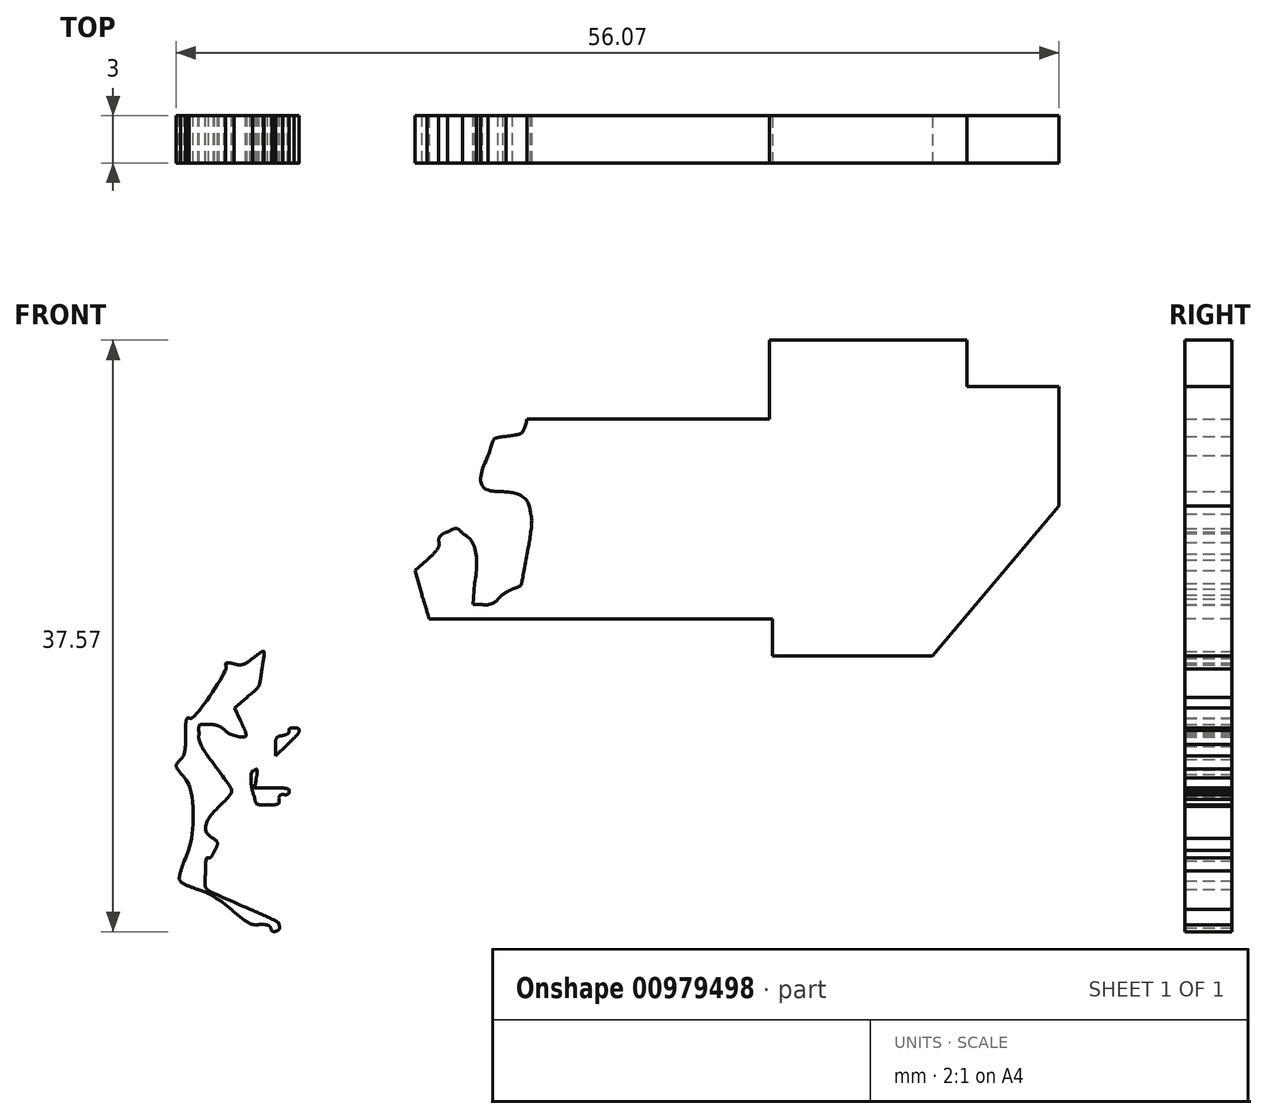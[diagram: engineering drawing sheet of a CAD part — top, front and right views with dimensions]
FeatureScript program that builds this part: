
annotation { "Feature Type Name" : "Feature", "Feature Type Description" : "" }
export const myFeature = defineFeature(function(context is Context, id is Id, definition is map)
    precondition{}
    {
        {
            var Q0;
            Q0=qCreatedBy(makeId("Front.planeOp"),FACE);
            var sketch = newSketch(context, id + "F0", { "sketchPlane" : qUnion([Q0])});
            skLineSegment(sketch, "E0", {"start": v(-32.88, 19.2) * mm, "end": v(-32.1, 20.83) * mm});
            skLineSegment(sketch, "E1", {"start": v(-32.1, 20.83) * mm, "end": v(-32.57, 22.16) * mm});
            skLineSegment(sketch, "E2", {"start": v(-27.5, 16.63) * mm, "end": v(-26.83, 16.28) * mm});
            skLineSegment(sketch, "E3", {"start": v(-26.83, 16.28) * mm, "end": v(-26.97, 16.83) * mm});
            skLineSegment(sketch, "E4", {"start": v(-24.85, 15.67) * mm, "end": v(-25.4, 15.88) * mm});
            skLineSegment(sketch, "E5", {"start": v(-25.4, 15.88) * mm, "end": v(-25.34, 18.4) * mm});
            skLineSegment(sketch, "E6", {"start": v(-1.75, 78.04) * mm, "end": v(-0.2, 79.6) * mm});
            skLineSegment(sketch, "E7", {"start": v(-0.2, 79.6) * mm, "end": v(1.27, 79.6) * mm});
            skLineSegment(sketch, "E8", {"start": v(38.3, 44.26) * mm, "end": v(38.3, 43.17) * mm});
            skLineSegment(sketch, "E9", {"start": v(38.3, 43.17) * mm, "end": v(37.62, 43.24) * mm});
            skLineSegment(sketch, "E10", {"start": v(39.65, -31.25) * mm, "end": v(39.52, -33.83) * mm});
            skLineSegment(sketch, "E11", {"start": v(39.52, -33.83) * mm, "end": v(40.18, -34.42) * mm});
            skLineSegment(sketch, "E12", {"start": v(1.4, 79.08) * mm, "end": v(0.3, 79.22) * mm});
            skLineSegment(sketch, "E13", {"start": v(0.3, 79.22) * mm, "end": v(-1.23, 77.67) * mm});
            skLineSegment(sketch, "E14", {"start": v(-12.51, 69.45) * mm, "end": v(-13.4, 69.45) * mm});
            skLineSegment(sketch, "E15", {"start": v(-13.4, 69.45) * mm, "end": v(-13.27, 67.07) * mm});
            skLineSegment(sketch, "E16", {"start": v(-18.31, 54.9) * mm, "end": v(-18.88, 53.48) * mm});
            skLineSegment(sketch, "E17", {"start": v(-18.88, 53.48) * mm, "end": v(-18.43, 53.1) * mm});
            skLineSegment(sketch, "E18", {"start": v(-20.94, 40.45) * mm, "end": v(-21.55, 40.45) * mm});
            skLineSegment(sketch, "E19", {"start": v(-21.55, 40.45) * mm, "end": v(-21.44, 41.8) * mm});
            skLineSegment(sketch, "E20", {"start": v(-24.47, 43.3) * mm, "end": v(-25.23, 42.61) * mm});
            skLineSegment(sketch, "E21", {"start": v(-25.23, 42.61) * mm, "end": v(-24.8, 41.05) * mm});
            skLineSegment(sketch, "E22", {"start": v(-37.96, -16.18) * mm, "end": v(-37.29, -17.23) * mm});
            skLineSegment(sketch, "E23", {"start": v(-37.29, -17.23) * mm, "end": v(-37.41, -20.41) * mm});
            skLineSegment(sketch, "E24", {"start": v(-30.4, -60.92) * mm, "end": v(-31.42, -62.04) * mm});
            skLineSegment(sketch, "E25", {"start": v(-31.42, -62.04) * mm, "end": v(-30.9, -63.02) * mm});
            skLineSegment(sketch, "E26", {"start": v(-36.35, 33.14) * mm, "end": v(-36.7, 33.88) * mm});
            skLineSegment(sketch, "E27", {"start": v(-36.7, 33.88) * mm, "end": v(-35.92, 34.57) * mm});
            skLineSegment(sketch, "E28", {"start": v(-34.09, 31.43) * mm, "end": v(-34.09, 30.84) * mm});
            skLineSegment(sketch, "E29", {"start": v(-34.09, 30.84) * mm, "end": v(-33.35, 31.56) * mm});
            skFitSpline(sketch, "E30", {"points": [v(-13.45, -80.7) * mm, v(-14.26, -80.4) * mm, v(-15.79, -79.86) * mm, v(-16.84, -79.51) * mm]});
            skFitSpline(sketch, "E31", {"points": [v(-16.84, -79.51) * mm, v(-20.43, -78.33) * mm, v(-20.6, -78.25) * mm, v(-21.55, -77.26) * mm]});
            skFitSpline(sketch, "E32", {"points": [v(-21.55, -77.26) * mm, v(-22.07, -76.72) * mm, v(-23.66, -74.52) * mm, v(-25.09, -72.37) * mm]});
            skFitSpline(sketch, "E33", {"points": [v(-25.09, -72.37) * mm, v(-26.52, -70.21) * mm, v(-28.36, -67.6) * mm, v(-29.19, -66.55) * mm]});
            skFitSpline(sketch, "E34", {"points": [v(-29.19, -66.55) * mm, v(-30.6, -64.76) * mm, v(-31.97, -62.53) * mm, v(-31.97, -62.03) * mm]});
            skFitSpline(sketch, "E35", {"points": [v(-31.97, -62.03) * mm, v(-31.97, -61.91) * mm, v(-31.5, -61.27) * mm, v(-30.92, -60.6) * mm]});
            skFitSpline(sketch, "E36", {"points": [v(-30.92, -60.6) * mm, v(-29.85, -59.39) * mm, v(-29, -57.92) * mm, v(-29, -57.28) * mm]});
            skFitSpline(sketch, "E37", {"points": [v(-29, -57.28) * mm, v(-29, -57.08) * mm, v(-29.34, -56.3) * mm, v(-29.75, -55.53) * mm]});
            skFitSpline(sketch, "E38", {"points": [v(-29.75, -55.53) * mm, v(-30.57, -53.98) * mm, v(-30.63, -53.57) * mm, v(-30.2, -52.72) * mm]});
            skFitSpline(sketch, "E39", {"points": [v(-30.2, -52.72) * mm, v(-29.95, -52.26) * mm, v(-29.92, -51.55) * mm, v(-30.04, -49.29) * mm]});
            skFitSpline(sketch, "E40", {"points": [v(-30.04, -49.29) * mm, v(-30.2, -46.13) * mm, v(-30.12, -46.32) * mm, v(-32.34, -43.6) * mm]});
            skFitSpline(sketch, "E41", {"points": [v(-32.34, -43.6) * mm, v(-32.83, -43) * mm, v(-33.38, -42.01) * mm, v(-33.55, -41.42) * mm]});
            skFitSpline(sketch, "E42", {"points": [v(-33.55, -41.42) * mm, v(-33.73, -40.84) * mm, v(-34.2, -39.94) * mm, v(-34.62, -39.44) * mm]});
            skFitSpline(sketch, "E43", {"points": [v(-34.62, -39.44) * mm, v(-36.03, -37.71) * mm, v(-36.52, -35.97) * mm, v(-35.98, -34.56) * mm]});
            skFitSpline(sketch, "E44", {"points": [v(-35.98, -34.56) * mm, v(-35.86, -34.24) * mm, v(-35.38, -33.57) * mm, v(-34.92, -33.07) * mm]});
            skFitSpline(sketch, "E45", {"points": [v(-34.92, -33.07) * mm, v(-33.97, -32.03) * mm, v(-34, -32.17) * mm, v(-34.37, -30.78) * mm]});
            skFitSpline(sketch, "E46", {"points": [v(-34.37, -30.78) * mm, v(-34.75, -29.38) * mm, v(-35.2, -28.53) * mm, v(-36.46, -26.88) * mm]});
            skFitSpline(sketch, "E47", {"points": [v(-36.46, -26.88) * mm, v(-37.04, -26.13) * mm, v(-37.61, -25.27) * mm, v(-37.73, -24.97) * mm]});
            skFitSpline(sketch, "E48", {"points": [v(-37.73, -24.97) * mm, v(-37.97, -24.39) * mm, v(-38.06, -21.07) * mm, v(-37.9, -18.8) * mm]});
            skFitSpline(sketch, "E49", {"points": [v(-37.9, -18.8) * mm, v(-37.82, -17.55) * mm, v(-37.87, -17.35) * mm, v(-38.39, -16.67) * mm]});
            skFitSpline(sketch, "E50", {"points": [v(-38.39, -16.67) * mm, v(-39.51, -15.19) * mm, v(-39.6, -12.77) * mm, v(-38.72, -7.81) * mm]});
            skFitSpline(sketch, "E51", {"points": [v(-38.72, -7.81) * mm, v(-38.24, -5.14) * mm, v(-38.31, -2.1) * mm, v(-38.87, -1) * mm]});
            skFitSpline(sketch, "E52", {"points": [v(-38.87, -1) * mm, v(-39.1, -0.56) * mm, v(-39.11, -0.29) * mm, v(-38.94, 0.17) * mm]});
            skFitSpline(sketch, "E53", {"points": [v(-38.94, 0.17) * mm, v(-38.62, 1) * mm, v(-38.87, 3.38) * mm, v(-39.5, 5.38) * mm]});
            skFitSpline(sketch, "E54", {"points": [v(-39.5, 5.38) * mm, v(-39.78, 6.29) * mm, v(-40.01, 7.26) * mm, v(-40.01, 7.54) * mm]});
            skFitSpline(sketch, "E55", {"points": [v(-40.01, 7.54) * mm, v(-40.01, 7.83) * mm, v(-39.68, 9.05) * mm, v(-39.27, 10.27) * mm]});
            skFitSpline(sketch, "E56", {"points": [v(-39.27, 10.27) * mm, v(-38.41, 12.85) * mm, v(-38.39, 13.06) * mm, v(-38.96, 13.2) * mm]});
            skFitSpline(sketch, "E57", {"points": [v(-38.96, 13.2) * mm, v(-39.71, 13.4) * mm, v(-39.48, 14.32) * mm, v(-38.38, 15.5) * mm]});
            skFitSpline(sketch, "E58", {"points": [v(-38.38, 15.5) * mm, v(-36.83, 17.16) * mm, v(-35.68, 17.57) * mm, v(-34.74, 16.8) * mm]});
            skFitSpline(sketch, "E59", {"points": [v(-34.74, 16.8) * mm, v(-34.08, 16.26) * mm, v(-32.77, 13.22) * mm, v(-32.66, 11.98) * mm]});
            skFitSpline(sketch, "E60", {"points": [v(-32.66, 11.98) * mm, v(-32.55, 10.86) * mm, v(-32.37, 10.61) * mm, v(-31.6, 10.6) * mm]});
            skFitSpline(sketch, "E61", {"points": [v(-31.6, 10.6) * mm, v(-31, 10.6) * mm, v(-30.96, 11.24) * mm, v(-31.55, 11.77) * mm]});
            skFitSpline(sketch, "E62", {"points": [v(-31.55, 11.77) * mm, v(-31.84, 12.03) * mm, v(-31.97, 12.42) * mm, v(-31.97, 13) * mm]});
            skFitSpline(sketch, "E63", {"points": [v(-31.97, 13) * mm, v(-31.97, 14.32) * mm, v(-32.62, 16.12) * mm, v(-33.18, 16.38) * mm]});
            skFitSpline(sketch, "E64", {"points": [v(-33.18, 16.38) * mm, v(-33.86, 16.69) * mm, v(-33.8, 17.27) * mm, v(-32.88, 19.2) * mm]});
            skFitSpline(sketch, "E65", {"points": [v(-32.57, 22.16) * mm, v(-32.82, 22.9) * mm, v(-33.03, 23.65) * mm, v(-33.03, 23.83) * mm]});
            skFitSpline(sketch, "E66", {"points": [v(-33.03, 23.83) * mm, v(-33.03, 24.1) * mm, v(-33.14, 24.14) * mm, v(-33.5, 24.01) * mm]});
            skFitSpline(sketch, "E67", {"points": [v(-33.5, 24.01) * mm, v(-33.77, 23.92) * mm, v(-34.4, 23.84) * mm, v(-34.93, 23.84) * mm]});
            skFitSpline(sketch, "E68", {"points": [v(-34.93, 23.84) * mm, v(-35.84, 23.83) * mm, v(-35.89, 23.86) * mm, v(-35.95, 24.48) * mm]});
            skFitSpline(sketch, "E69", {"points": [v(-35.95, 24.48) * mm, v(-36.05, 25.55) * mm, v(-34.78, 26.27) * mm, v(-32.78, 26.27) * mm]});
            skFitSpline(sketch, "E70", {"points": [v(-32.78, 26.27) * mm, v(-31.93, 26.27) * mm, v(-31.64, 26.16) * mm, v(-31.1, 25.65) * mm]});
            skFitSpline(sketch, "E71", {"points": [v(-31.1, 25.65) * mm, v(-30.75, 25.3) * mm, v(-30.32, 25.08) * mm, v(-30.15, 25.14) * mm]});
            skFitSpline(sketch, "E72", {"points": [v(-30.15, 25.14) * mm, v(-29.7, 25.31) * mm, v(-29.77, 25.47) * mm, v(-30.7, 26.37) * mm]});
            skFitSpline(sketch, "E73", {"points": [v(-30.7, 26.37) * mm, v(-31.5, 27.15) * mm, v(-31.55, 27.27) * mm, v(-31.55, 28.43) * mm]});
            skFitSpline(sketch, "E74", {"points": [v(-31.55, 28.43) * mm, v(-31.55, 29.6) * mm, v(-31.52, 29.65) * mm, v(-31.02, 29.65) * mm]});
            skFitSpline(sketch, "E75", {"points": [v(-31.02, 29.65) * mm, v(-30.7, 29.65) * mm, v(-30.49, 29.53) * mm, v(-30.49, 29.36) * mm]});
            skFitSpline(sketch, "E76", {"points": [v(-30.49, 29.36) * mm, v(-30.49, 28.94) * mm, v(-28.82, 27.75) * mm, v(-28.24, 27.75) * mm]});
            skFitSpline(sketch, "E77", {"points": [v(-28.24, 27.75) * mm, v(-27.83, 27.75) * mm, v(-27.75, 27.6) * mm, v(-27.62, 26.6) * mm]});
            skFitSpline(sketch, "E78", {"points": [v(-27.62, 26.6) * mm, v(-27.46, 25.26) * mm, v(-27.66, 24.55) * mm, v(-28.57, 23.22) * mm]});
            skFitSpline(sketch, "E79", {"points": [v(-28.57, 23.22) * mm, v(-29.21, 22.29) * mm, v(-29.4, 21.61) * mm, v(-29.02, 21.61) * mm]});
            skFitSpline(sketch, "E80", {"points": [v(-29.02, 21.61) * mm, v(-28.66, 21.61) * mm, v(-28.35, 20.18) * mm, v(-28.49, 19.14) * mm]});
            skFitSpline(sketch, "E81", {"points": [v(-28.49, 19.14) * mm, v(-28.66, 17.84) * mm, v(-28.36, 17.07) * mm, v(-27.5, 16.63) * mm]});
            skFitSpline(sketch, "E82", {"points": [v(-26.97, 16.83) * mm, v(-27.1, 17.33) * mm, v(-27.05, 17.38) * mm, v(-26.5, 17.38) * mm]});
            skFitSpline(sketch, "E83", {"points": [v(-26.5, 17.38) * mm, v(-25.81, 17.38) * mm, v(-25.62, 17.08) * mm, v(-25.62, 16.04) * mm]});
            skFitSpline(sketch, "E84", {"points": [v(-25.62, 16.04) * mm, v(-25.62, 15.5) * mm, v(-25.82, 15.19) * mm, v(-26.56, 14.52) * mm]});
            skFitSpline(sketch, "E85", {"points": [v(-26.56, 14.52) * mm, v(-27.09, 14.05) * mm, v(-27.58, 13.4) * mm, v(-27.66, 13.06) * mm]});
            skFitSpline(sketch, "E86", {"points": [v(-27.66, 13.06) * mm, v(-27.79, 12.49) * mm, v(-27.76, 12.45) * mm, v(-27.3, 12.58) * mm]});
            skFitSpline(sketch, "E87", {"points": [v(-27.3, 12.58) * mm, v(-27.01, 12.65) * mm, v(-26.47, 12.72) * mm, v(-26.09, 12.72) * mm]});
            skFitSpline(sketch, "E88", {"points": [v(-26.09, 12.72) * mm, v(-25.47, 12.72) * mm, v(-25.42, 12.76) * mm, v(-25.61, 13.13) * mm]});
            skFitSpline(sketch, "E89", {"points": [v(-25.61, 13.13) * mm, v(-26.02, 13.88) * mm, v(-25.88, 14.6) * mm, v(-25.31, 14.75) * mm]});
            skFitSpline(sketch, "E90", {"points": [v(-25.31, 14.75) * mm, v(-25.03, 14.82) * mm, v(-24.68, 15.01) * mm, v(-24.55, 15.17) * mm]});
            skFitSpline(sketch, "E91", {"points": [v(-24.55, 15.17) * mm, v(-24.35, 15.4) * mm, v(-24.42, 15.5) * mm, v(-24.85, 15.67) * mm]});
            skFitSpline(sketch, "E92", {"points": [v(-25.34, 18.4) * mm, v(-25.28, 20.49) * mm, v(-25.2, 21.05) * mm, v(-24.84, 21.66) * mm]});
            skFitSpline(sketch, "E93", {"points": [v(-24.84, 21.66) * mm, v(-24.6, 22.07) * mm, v(-24.33, 22.91) * mm, v(-24.25, 23.54) * mm]});
            skFitSpline(sketch, "E94", {"points": [v(-24.25, 23.54) * mm, v(-24.05, 24.98) * mm, v(-23.67, 25.42) * mm, v(-22.64, 25.42) * mm]});
            skFitSpline(sketch, "E95", {"points": [v(-22.64, 25.42) * mm, v(-21.97, 25.42) * mm, v(-21.73, 25.28) * mm, v(-21.09, 24.54) * mm]});
            skFitSpline(sketch, "E96", {"points": [v(-21.09, 24.54) * mm, v(-20.67, 24.05) * mm, v(-20.32, 23.55) * mm, v(-20.32, 23.43) * mm]});
            skFitSpline(sketch, "E97", {"points": [v(-20.32, 23.43) * mm, v(-20.3, 22.93) * mm, v(-19.5, 25.15) * mm, v(-19.5, 25.74) * mm]});
            skFitSpline(sketch, "E98", {"points": [v(-19.5, 25.74) * mm, v(-19.48, 26.68) * mm, v(-19.75, 27) * mm, v(-20.27, 26.68) * mm]});
            skFitSpline(sketch, "E99", {"points": [v(-20.27, 26.68) * mm, v(-20.84, 26.32) * mm, v(-23.7, 26.75) * mm, v(-24.99, 27.38) * mm]});
            skFitSpline(sketch, "E100", {"points": [v(-24.99, 27.38) * mm, v(-26.7, 28.23) * mm, v(-27.27, 29.95) * mm, v(-26.55, 32.07) * mm]});
            skFitSpline(sketch, "E101", {"points": [v(-26.55, 32.07) * mm, v(-26.23, 33) * mm, v(-26.23, 33.13) * mm, v(-26.58, 33.9) * mm]});
            skFitSpline(sketch, "E102", {"points": [v(-26.58, 33.9) * mm, v(-27.04, 34.91) * mm, v(-26.9, 36) * mm, v(-26.2, 36.92) * mm]});
            skFitSpline(sketch, "E103", {"points": [v(-26.2, 36.92) * mm, v(-24.96, 38.54) * mm, v(-24.76, 39.42) * mm, v(-25.3, 40.73) * mm]});
            skFitSpline(sketch, "E104", {"points": [v(-25.3, 40.73) * mm, v(-25.48, 41.15) * mm, v(-25.62, 41.87) * mm, v(-25.62, 42.33) * mm]});
            skFitSpline(sketch, "E105", {"points": [v(-25.62, 42.33) * mm, v(-25.62, 43.02) * mm, v(-25.5, 43.25) * mm, v(-24.99, 43.62) * mm]});
            skFitSpline(sketch, "E106", {"points": [v(-24.99, 43.62) * mm, v(-24.64, 43.87) * mm, v(-24.35, 44.26) * mm, v(-24.35, 44.48) * mm]});
            skFitSpline(sketch, "E107", {"points": [v(-24.35, 44.48) * mm, v(-24.35, 45.6) * mm, v(-22.43, 46.16) * mm, v(-21.62, 45.29) * mm]});
            skFitSpline(sketch, "E108", {"points": [v(-21.62, 45.29) * mm, v(-21.1, 44.74) * mm, v(-20.66, 42.78) * mm, v(-20.82, 41.8) * mm]});
            skFitSpline(sketch, "E109", {"points": [v(-20.82, 41.8) * mm, v(-20.95, 40.98) * mm, v(-20.5, 40.8) * mm, v(-20.12, 41.5) * mm]});
            skFitSpline(sketch, "E110", {"points": [v(-20.12, 41.5) * mm, v(-20, 41.74) * mm, v(-19.7, 41.93) * mm, v(-19.48, 41.93) * mm]});
            skFitSpline(sketch, "E111", {"points": [v(-19.48, 41.93) * mm, v(-19.2, 41.93) * mm, v(-19.03, 42.12) * mm, v(-18.95, 42.51) * mm]});
            skFitSpline(sketch, "E112", {"points": [v(-18.95, 42.51) * mm, v(-18.9, 42.83) * mm, v(-18.75, 43.5) * mm, v(-18.63, 44) * mm]});
            skFitSpline(sketch, "E113", {"points": [v(-18.63, 44) * mm, v(-18.15, 46.1) * mm, v(-18.46, 46.83) * mm, v(-19.95, 47.1) * mm]});
            skFitSpline(sketch, "E114", {"points": [v(-19.95, 47.1) * mm, v(-21.37, 47.35) * mm, v(-21.68, 48.31) * mm, v(-21.02, 50.45) * mm]});
            skFitSpline(sketch, "E115", {"points": [v(-21.02, 50.45) * mm, v(-20.67, 51.58) * mm, v(-20.6, 51.66) * mm, v(-20, 51.67) * mm]});
            skFitSpline(sketch, "E116", {"points": [v(-20, 51.67) * mm, v(-19.64, 51.67) * mm, v(-19.17, 51.8) * mm, v(-18.94, 51.97) * mm]});
            skFitSpline(sketch, "E117", {"points": [v(-18.94, 51.97) * mm, v(-18.56, 52.25) * mm, v(-18.55, 52.28) * mm, v(-18.9, 52.67) * mm]});
            skFitSpline(sketch, "E118", {"points": [v(-18.9, 52.67) * mm, v(-19.36, 53.18) * mm, v(-19.37, 53.99) * mm, v(-18.93, 55) * mm]});
            skFitSpline(sketch, "E119", {"points": [v(-18.93, 55) * mm, v(-18.26, 56.57) * mm, v(-18.22, 56.96) * mm, v(-18.55, 58.71) * mm]});
            skFitSpline(sketch, "E120", {"points": [v(-18.55, 58.71) * mm, v(-19.05, 61.35) * mm, v(-18.66, 63.1) * mm, v(-17.57, 63.1) * mm]});
            skFitSpline(sketch, "E121", {"points": [v(-17.57, 63.1) * mm, v(-17.13, 63.1) * mm, v(-16.93, 62.86) * mm, v(-16.62, 61.94) * mm]});
            skFitSpline(sketch, "E122", {"points": [v(-16.62, 61.94) * mm, v(-16.19, 60.62) * mm, v(-15.25, 61.36) * mm, v(-15.25, 63.03) * mm]});
            skFitSpline(sketch, "E123", {"points": [v(-15.25, 63.03) * mm, v(-15.25, 63.72) * mm, v(-15.21, 63.77) * mm, v(-14.72, 63.65) * mm]});
            skFitSpline(sketch, "E124", {"points": [v(-14.72, 63.65) * mm, v(-13.88, 63.44) * mm, v(-13.7, 64.21) * mm, v(-13.86, 67.25) * mm]});
            skFitSpline(sketch, "E125", {"points": [v(-13.86, 67.25) * mm, v(-14.01, 70.15) * mm, v(-14.06, 70.07) * mm, v(-12.21, 70.08) * mm]});
            skFitSpline(sketch, "E126", {"points": [v(-12.21, 70.08) * mm, v(-11.52, 70.08) * mm, v(-11.25, 70.23) * mm, v(-10.4, 71.12) * mm]});
            skFitSpline(sketch, "E127", {"points": [v(-10.4, 71.12) * mm, v(-9.38, 72.18) * mm, v(-9.03, 72.34) * mm, v(-6.52, 72.84) * mm]});
            skFitSpline(sketch, "E128", {"points": [v(-6.52, 72.84) * mm, v(-4.93, 73.15) * mm, v(-4.21, 73.78) * mm, v(-3.7, 75.27) * mm]});
            skFitSpline(sketch, "E129", {"points": [v(-3.7, 75.27) * mm, v(-3.38, 76.2) * mm, v(-2.96, 76.8) * mm, v(-1.75, 78.04) * mm]});
            skFitSpline(sketch, "E130", {"points": [v(1.27, 79.6) * mm, v(2.66, 79.6) * mm, v(2.79, 79.65) * mm, v(3.57, 80.36) * mm]});
            skFitSpline(sketch, "E131", {"points": [v(3.57, 80.36) * mm, v(4.72, 81.4) * mm, v(5.62, 81.51) * mm, v(6.84, 80.8) * mm]});
            skFitSpline(sketch, "E132", {"points": [v(6.84, 80.8) * mm, v(7.4, 80.48) * mm, v(8.11, 80.24) * mm, v(8.56, 80.24) * mm]});
            skFitSpline(sketch, "E133", {"points": [v(8.56, 80.24) * mm, v(9.65, 80.24) * mm, v(10.66, 79.76) * mm, v(12.03, 78.58) * mm]});
            skFitSpline(sketch, "E134", {"points": [v(12.03, 78.58) * mm, v(12.68, 78.02) * mm, v(13.76, 77.21) * mm, v(14.43, 76.8) * mm]});
            skFitSpline(sketch, "E135", {"points": [v(14.43, 76.8) * mm, v(16.07, 75.75) * mm, v(16.3, 75.23) * mm, v(16.26, 72.68) * mm]});
            skFitSpline(sketch, "E136", {"points": [v(16.26, 72.68) * mm, v(16.21, 70.3) * mm, v(16.3, 70.06) * mm, v(17.99, 67.97) * mm]});
            skFitSpline(sketch, "E137", {"points": [v(17.99, 67.97) * mm, v(19.34, 66.28) * mm, v(19.58, 65.73) * mm, v(19.78, 63.84) * mm]});
            skFitSpline(sketch, "E138", {"points": [v(19.78, 63.84) * mm, v(19.97, 61.97) * mm, v(20.1, 61.75) * mm, v(21.2, 61.28) * mm]});
            skFitSpline(sketch, "E139", {"points": [v(21.2, 61.28) * mm, v(21.95, 60.97) * mm, v(22.77, 60.9) * mm, v(25.95, 60.87) * mm]});
            skFitSpline(sketch, "E140", {"points": [v(25.95, 60.87) * mm, v(29.47, 60.83) * mm, v(29.87, 60.8) * mm, v(30.78, 60.35) * mm]});
            skFitSpline(sketch, "E141", {"points": [v(30.78, 60.35) * mm, v(31.33, 60.09) * mm, v(31.82, 59.71) * mm, v(31.88, 59.53) * mm]});
            skFitSpline(sketch, "E142", {"points": [v(31.88, 59.53) * mm, v(32.1, 58.78) * mm, v(32.32, 58.58) * mm, v(33.34, 58.19) * mm]});
            skFitSpline(sketch, "E143", {"points": [v(33.34, 58.19) * mm, v(35, 57.54) * mm, v(35.47, 56.96) * mm, v(35.61, 55.41) * mm]});
            skFitSpline(sketch, "E144", {"points": [v(35.61, 55.41) * mm, v(35.68, 54.7) * mm, v(35.93, 53.67) * mm, v(36.17, 53.15) * mm]});
            skFitSpline(sketch, "E145", {"points": [v(36.17, 53.15) * mm, v(36.4, 52.63) * mm, v(36.6, 51.94) * mm, v(36.6, 51.62) * mm]});
            skFitSpline(sketch, "E146", {"points": [v(36.6, 51.62) * mm, v(36.6, 51.3) * mm, v(36.8, 50.55) * mm, v(37.02, 49.93) * mm]});
            skFitSpline(sketch, "E147", {"points": [v(37.02, 49.93) * mm, v(37.7, 48.08) * mm, v(38.3, 45.42) * mm, v(38.3, 44.26) * mm]});
            skFitSpline(sketch, "E148", {"points": [v(37.62, 43.24) * mm, v(36.87, 43.31) * mm, v(36.86, 43.33) * mm, v(36.05, 46.9) * mm]});
            skFitSpline(sketch, "E149", {"points": [v(36.05, 46.9) * mm, v(35.75, 48.23) * mm, v(35.65, 48.45) * mm, v(35.6, 47.92) * mm]});
            skFitSpline(sketch, "E150", {"points": [v(35.6, 47.92) * mm, v(35.56, 47.55) * mm, v(35.72, 46.61) * mm, v(35.96, 45.84) * mm]});
            skFitSpline(sketch, "E151", {"points": [v(35.96, 45.84) * mm, v(36.2, 45.06) * mm, v(36.4, 44.16) * mm, v(36.4, 43.83) * mm]});
            skFitSpline(sketch, "E152", {"points": [v(36.4, 43.83) * mm, v(36.4, 42.72) * mm, v(36.23, 42.57) * mm, v(35.04, 42.57) * mm]});
            skFitSpline(sketch, "E153", {"points": [v(35.04, 42.57) * mm, v(34.35, 42.57) * mm, v(33.78, 42.44) * mm, v(33.53, 42.23) * mm]});
            skFitSpline(sketch, "E154", {"points": [v(33.53, 42.23) * mm, v(33.14, 41.92) * mm, v(33.15, 41.9) * mm, v(33.78, 42.01) * mm]});
            skFitSpline(sketch, "E155", {"points": [v(33.78, 42.01) * mm, v(34.37, 42.1) * mm, v(34.48, 42.05) * mm, v(34.7, 41.5) * mm]});
            skFitSpline(sketch, "E156", {"points": [v(34.7, 41.5) * mm, v(35.23, 40.23) * mm, v(34.46, 39.89) * mm, v(32.77, 40.66) * mm]});
            skFitSpline(sketch, "E157", {"points": [v(32.77, 40.66) * mm, v(30, 41.91) * mm, v(30.46, 40.26) * mm, v(33.3, 38.77) * mm]});
            skFitSpline(sketch, "E158", {"points": [v(33.3, 38.77) * mm, v(34.7, 38.04) * mm, v(35.03, 37.98) * mm, v(35.2, 38.44) * mm]});
            skFitSpline(sketch, "E159", {"points": [v(35.2, 38.44) * mm, v(35.4, 38.97) * mm, v(36.94, 38.86) * mm, v(37.34, 38.29) * mm]});
            skFitSpline(sketch, "E160", {"points": [v(37.34, 38.29) * mm, v(37.8, 37.64) * mm, v(37.75, 36.5) * mm, v(37.25, 35.69) * mm]});
            skFitSpline(sketch, "E161", {"points": [v(37.25, 35.69) * mm, v(37.01, 35.31) * mm, v(36.68, 34.6) * mm, v(36.5, 34.09) * mm]});
            skFitSpline(sketch, "E162", {"points": [v(36.5, 34.09) * mm, v(36.07, 32.87) * mm, v(35.62, 32.4) * mm, v(34.86, 32.4) * mm]});
            skFitSpline(sketch, "E163", {"points": [v(34.86, 32.4) * mm, v(34.06, 32.4) * mm, v(32.85, 32.98) * mm, v(32.57, 33.5) * mm]});
            skFitSpline(sketch, "E164", {"points": [v(32.57, 33.5) * mm, v(32.35, 33.9) * mm, v(32.37, 33.91) * mm, v(33.4, 34.23) * mm]});
            skFitSpline(sketch, "E165", {"points": [v(33.4, 34.23) * mm, v(33.55, 34.27) * mm, v(33.64, 34.43) * mm, v(33.6, 34.58) * mm]});
            skFitSpline(sketch, "E166", {"points": [v(33.6, 34.58) * mm, v(33.47, 34.97) * mm, v(32.1, 35.02) * mm, v(31.26, 34.66) * mm]});
            skFitSpline(sketch, "E167", {"points": [v(31.26, 34.66) * mm, v(30.63, 34.4) * mm, v(30.54, 34.27) * mm, v(30.63, 33.8) * mm]});
            skFitSpline(sketch, "E168", {"points": [v(30.63, 33.8) * mm, v(30.71, 33.37) * mm, v(30.83, 33.27) * mm, v(31.13, 33.37) * mm]});
            skFitSpline(sketch, "E169", {"points": [v(31.13, 33.37) * mm, v(31.68, 33.54) * mm, v(31.8, 33.13) * mm, v(31.57, 31.7) * mm]});
            skFitSpline(sketch, "E170", {"points": [v(31.57, 31.7) * mm, v(31.47, 31.04) * mm, v(31.4, 30.5) * mm, v(31.43, 30.5) * mm]});
            skFitSpline(sketch, "E171", {"points": [v(31.43, 30.5) * mm, v(31.46, 30.5) * mm, v(31.82, 30.65) * mm, v(32.25, 30.82) * mm]});
            skFitSpline(sketch, "E172", {"points": [v(32.25, 30.82) * mm, v(33.01, 31.14) * mm, v(33.02, 31.14) * mm, v(33.26, 30.56) * mm]});
            skFitSpline(sketch, "E173", {"points": [v(33.26, 30.56) * mm, v(33.39, 30.24) * mm, v(33.5, 29.43) * mm, v(33.52, 28.77) * mm]});
            skFitSpline(sketch, "E174", {"points": [v(33.52, 28.77) * mm, v(33.55, 27.14) * mm, v(33.03, 26.57) * mm, v(31.4, 26.43) * mm]});
            skFitSpline(sketch, "E175", {"points": [v(31.4, 26.43) * mm, v(29.99, 26.32) * mm, v(29.27, 25.83) * mm, v(28.59, 24.5) * mm]});
            skFitSpline(sketch, "E176", {"points": [v(28.59, 24.5) * mm, v(28.09, 23.52) * mm, v(28.09, 23.5) * mm, v(28.46, 22.8) * mm]});
            skFitSpline(sketch, "E177", {"points": [v(28.46, 22.8) * mm, v(29.02, 21.76) * mm, v(28.8, 20.5) * mm, v(27.76, 18.77) * mm]});
            skFitSpline(sketch, "E178", {"points": [v(27.76, 18.77) * mm, v(26.26, 16.28) * mm, v(26.34, 15.6) * mm, v(28.5, 12.89) * mm]});
            skFitSpline(sketch, "E179", {"points": [v(28.5, 12.89) * mm, v(30.07, 10.9) * mm, v(30.64, 9.85) * mm, v(31.32, 7.7) * mm]});
            skFitSpline(sketch, "E180", {"points": [v(31.32, 7.7) * mm, v(31.79, 6.2) * mm, v(31.8, 6.14) * mm, v(31.41, 5.73) * mm]});
            skFitSpline(sketch, "E181", {"points": [v(31.41, 5.73) * mm, v(31.08, 5.36) * mm, v(31.06, 5.2) * mm, v(31.28, 4.6) * mm]});
            skFitSpline(sketch, "E182", {"points": [v(31.28, 4.6) * mm, v(31.65, 3.58) * mm, v(31.59, 2.92) * mm, v(31, 1.59) * mm]});
            skFitSpline(sketch, "E183", {"points": [v(31, 1.59) * mm, v(30.4, 0.22) * mm, v(30.37, 0) * mm, v(30.73, -0.98) * mm]});
            skFitSpline(sketch, "E184", {"points": [v(30.73, -0.98) * mm, v(30.96, -1.6) * mm, v(30.93, -1.79) * mm, v(30.48, -2.62) * mm]});
            skFitSpline(sketch, "E185", {"points": [v(30.48, -2.62) * mm, v(29.76, -3.92) * mm, v(30.03, -4.4) * mm, v(31.97, -5.39) * mm]});
            skFitSpline(sketch, "E186", {"points": [v(31.97, -5.39) * mm, v(33.32, -6.07) * mm, v(33.55, -6.12) * mm, v(34.1, -5.9) * mm]});
            skFitSpline(sketch, "E187", {"points": [v(34.1, -5.9) * mm, v(34.89, -5.57) * mm, v(35.48, -5.74) * mm, v(36.67, -6.64) * mm]});
            skFitSpline(sketch, "E188", {"points": [v(36.67, -6.64) * mm, v(37.21, -7.06) * mm, v(37.94, -7.45) * mm, v(38.28, -7.52) * mm]});
            skFitSpline(sketch, "E189", {"points": [v(38.28, -7.52) * mm, v(38.74, -7.61) * mm, v(38.97, -7.82) * mm, v(39.14, -8.29) * mm]});
            skFitSpline(sketch, "E190", {"points": [v(39.14, -8.29) * mm, v(39.46, -9.22) * mm, v(39.43, -9.36) * mm, v(38.73, -10.24) * mm]});
            skFitSpline(sketch, "E191", {"points": [v(38.73, -10.24) * mm, v(37.95, -11.22) * mm, v(37.9, -12.13) * mm, v(38.57, -13.12) * mm]});
            skFitSpline(sketch, "E192", {"points": [v(38.57, -13.12) * mm, v(38.94, -13.67) * mm, v(39.23, -13.86) * mm, v(39.79, -13.91) * mm]});
            skFitSpline(sketch, "E193", {"points": [v(39.79, -13.91) * mm, v(40.2, -13.95) * mm, v(40.6, -14.1) * mm, v(40.68, -14.23) * mm]});
            skFitSpline(sketch, "E194", {"points": [v(40.68, -14.23) * mm, v(40.98, -14.7) * mm, v(40.84, -15.58) * mm, v(40.4, -15.98) * mm]});
            skFitSpline(sketch, "E195", {"points": [v(40.4, -15.98) * mm, v(40.04, -16.3) * mm, v(39.97, -16.56) * mm, v(40.05, -17.26) * mm]});
            skFitSpline(sketch, "E196", {"points": [v(40.05, -17.26) * mm, v(40.14, -18.03) * mm, v(40.09, -18.17) * mm, v(39.65, -18.37) * mm]});
            skFitSpline(sketch, "E197", {"points": [v(39.65, -18.37) * mm, v(39.06, -18.64) * mm, v(39.03, -18.9) * mm, v(39.5, -20) * mm]});
            skFitSpline(sketch, "E198", {"points": [v(39.5, -20) * mm, v(39.77, -20.67) * mm, v(39.83, -21.57) * mm, v(39.81, -24.74) * mm]});
            skFitSpline(sketch, "E199", {"points": [v(39.81, -24.74) * mm, v(39.8, -26.9) * mm, v(39.73, -29.82) * mm, v(39.65, -31.25) * mm]});
            skFitSpline(sketch, "E200", {"points": [v(40.18, -34.42) * mm, v(40.54, -34.74) * mm, v(40.84, -35.18) * mm, v(40.84, -35.41) * mm]});
            skFitSpline(sketch, "E201", {"points": [v(40.84, -35.41) * mm, v(40.84, -36.27) * mm, v(39.96, -37.65) * mm, v(38.92, -38.41) * mm]});
            skFitSpline(sketch, "E202", {"points": [v(38.92, -38.41) * mm, v(37.63, -39.36) * mm, v(37.28, -40) * mm, v(37.05, -41.89) * mm]});
            skFitSpline(sketch, "E203", {"points": [v(37.05, -41.89) * mm, v(36.94, -42.7) * mm, v(36.66, -43.77) * mm, v(36.42, -44.27) * mm]});
            skFitSpline(sketch, "E204", {"points": [v(36.42, -44.27) * mm, v(35.96, -45.22) * mm, v(33.78, -47.87) * mm, v(31.3, -50.5) * mm]});
            skFitSpline(sketch, "E205", {"points": [v(31.3, -50.5) * mm, v(29.02, -52.92) * mm, v(27.8, -55.66) * mm, v(27.2, -59.77) * mm]});
            skFitSpline(sketch, "E206", {"points": [v(27.2, -59.77) * mm, v(26.85, -62.13) * mm, v(26.75, -62.37) * mm, v(25.14, -65) * mm]});
            skFitSpline(sketch, "E207", {"points": [v(25.14, -65) * mm, v(24.58, -65.91) * mm, v(24.35, -66.6) * mm, v(24.16, -67.9) * mm]});
            skFitSpline(sketch, "E208", {"points": [v(24.16, -67.9) * mm, v(23.88, -69.93) * mm, v(23.36, -71.03) * mm, v(22.29, -71.92) * mm]});
            skFitSpline(sketch, "E209", {"points": [v(22.29, -71.92) * mm, v(21.43, -72.63) * mm, v(19.94, -73.22) * mm, v(19, -73.22) * mm]});
            skFitSpline(sketch, "E210", {"points": [v(19, -73.22) * mm, v(18.6, -73.22) * mm, v(18.4, -73.32) * mm, v(18.4, -73.56) * mm]});
            skFitSpline(sketch, "E211", {"points": [v(18.4, -73.56) * mm, v(18.4, -73.75) * mm, v(18.21, -74.22) * mm, v(17.97, -74.6) * mm]});
            skFitSpline(sketch, "E212", {"points": [v(17.97, -74.6) * mm, v(17.57, -75.26) * mm, v(17.56, -75.35) * mm, v(17.87, -76.08) * mm]});
            skFitSpline(sketch, "E213", {"points": [v(17.87, -76.08) * mm, v(18.34, -77.22) * mm, v(18.3, -77.38) * mm, v(17.14, -78.58) * mm]});
            skFitSpline(sketch, "E214", {"points": [v(17.14, -78.58) * mm, v(16.56, -79.18) * mm, v(15.87, -79.93) * mm, v(15.6, -80.25) * mm]});
            skFitSpline(sketch, "E215", {"points": [v(15.6, -80.25) * mm, v(15.34, -80.56) * mm, v(14.86, -80.88) * mm, v(14.54, -80.96) * mm]});
            skFitSpline(sketch, "E216", {"points": [v(14.54, -80.96) * mm, v(14.03, -81.08) * mm, v(13.96, -81.03) * mm, v(13.96, -80.56) * mm]});
            skFitSpline(sketch, "E217", {"points": [v(13.96, -80.56) * mm, v(13.96, -80.25) * mm, v(13.75, -79.86) * mm, v(13.47, -79.63) * mm]});
            skFitSpline(sketch, "E218", {"points": [v(13.47, -79.63) * mm, v(12.33, -78.73) * mm, v(12.3, -77.45) * mm, v(13.44, -77.45) * mm]});
            skFitSpline(sketch, "E219", {"points": [v(13.44, -77.45) * mm, v(14.2, -77.45) * mm, v(15.11, -76) * mm, v(14.94, -75.07) * mm]});
            skFitSpline(sketch, "E220", {"points": [v(14.94, -75.07) * mm, v(14.87, -74.7) * mm, v(14.75, -74.02) * mm, v(14.67, -73.57) * mm]});
            skFitSpline(sketch, "E221", {"points": [v(14.67, -73.57) * mm, v(14.58, -73.02) * mm, v(14.45, -72.8) * mm, v(14.25, -72.88) * mm]});
            skFitSpline(sketch, "E222", {"points": [v(14.25, -72.88) * mm, v(14.1, -72.94) * mm, v(13.13, -72.88) * mm, v(12.11, -72.76) * mm]});
            skFitSpline(sketch, "E223", {"points": [v(12.11, -72.76) * mm, v(10.8, -72.6) * mm, v(10.12, -72.4) * mm, v(9.8, -72.1) * mm]});
            skFitSpline(sketch, "E224", {"points": [v(9.8, -72.1) * mm, v(9.32, -71.67) * mm, v(8.88, -71.75) * mm, v(8.88, -72.28) * mm]});
            skFitSpline(sketch, "E225", {"points": [v(8.88, -72.28) * mm, v(8.88, -72.66) * mm, v(8.5, -72.65) * mm, v(7.82, -72.26) * mm]});
            skFitSpline(sketch, "E226", {"points": [v(7.82, -72.26) * mm, v(7.11, -71.86) * mm, v(5.83, -71.87) * mm, v(4.94, -72.29) * mm]});
            skFitSpline(sketch, "E227", {"points": [v(4.94, -72.29) * mm, v(4.16, -72.66) * mm, v(4.18, -72.61) * mm, v(4.14, -74.27) * mm]});
            skFitSpline(sketch, "E228", {"points": [v(4.14, -74.27) * mm, v(4.12, -75.43) * mm, v(4.11, -75.44) * mm, v(3.17, -75.91) * mm]});
            skFitSpline(sketch, "E229", {"points": [v(3.17, -75.91) * mm, v(2.65, -76.18) * mm, v(1.84, -76.77) * mm, v(1.36, -77.24) * mm]});
            skFitSpline(sketch, "E230", {"points": [v(1.36, -77.24) * mm, v(0.68, -77.91) * mm, v(-0.19, -78.37) * mm, v(-2.67, -79.37) * mm]});
            skFitSpline(sketch, "E231", {"points": [v(-2.67, -79.37) * mm, v(-6.5, -80.92) * mm, v(-7.82, -81.25) * mm, v(-10.17, -81.25) * mm]});
            skFitSpline(sketch, "E232", {"points": [v(-10.17, -81.25) * mm, v(-11.59, -81.25) * mm, v(-12.28, -81.13) * mm, v(-13.45, -80.7) * mm]});
            skFitSpline(sketch, "E233", {"points": [v(-6.84, -80.3) * mm, v(-6.29, -80.14) * mm, v(-4.56, -79.5) * mm, v(-3, -78.88) * mm]});
            skFitSpline(sketch, "E234", {"points": [v(-3, -78.88) * mm, v(-0.66, -77.96) * mm, v(0.05, -77.57) * mm, v(1.08, -76.65) * mm]});
            skFitSpline(sketch, "E235", {"points": [v(1.08, -76.65) * mm, v(1.77, -76.04) * mm, v(2.46, -75.54) * mm, v(2.62, -75.54) * mm]});
            skFitSpline(sketch, "E236", {"points": [v(2.62, -75.54) * mm, v(2.78, -75.54) * mm, v(3.12, -75.37) * mm, v(3.38, -75.16) * mm]});
            skFitSpline(sketch, "E237", {"points": [v(3.38, -75.16) * mm, v(3.8, -74.81) * mm, v(3.83, -74.72) * mm, v(3.59, -73.93) * mm]});
            skFitSpline(sketch, "E238", {"points": [v(3.59, -73.93) * mm, v(3.4, -73.28) * mm, v(3.39, -72.96) * mm, v(3.57, -72.61) * mm]});
            skFitSpline(sketch, "E239", {"points": [v(3.57, -72.61) * mm, v(4.07, -71.69) * mm, v(6.12, -71.11) * mm, v(7.53, -71.5) * mm]});
            skFitSpline(sketch, "E240", {"points": [v(7.53, -71.5) * mm, v(8.17, -71.68) * mm, v(8.4, -71.66) * mm, v(8.68, -71.41) * mm]});
            skFitSpline(sketch, "E241", {"points": [v(8.68, -71.41) * mm, v(9.15, -70.98) * mm, v(9.64, -71.02) * mm, v(10.13, -71.54) * mm]});
            skFitSpline(sketch, "E242", {"points": [v(10.13, -71.54) * mm, v(10.44, -71.88) * mm, v(10.95, -72.03) * mm, v(12.2, -72.17) * mm]});
            skFitSpline(sketch, "E243", {"points": [v(12.2, -72.17) * mm, v(13.1, -72.28) * mm, v(14, -72.32) * mm, v(14.17, -72.26) * mm]});
            skFitSpline(sketch, "E244", {"points": [v(14.17, -72.26) * mm, v(14.75, -72.09) * mm, v(15.04, -72.5) * mm, v(15.33, -73.91) * mm]});
            skFitSpline(sketch, "E245", {"points": [v(15.33, -73.91) * mm, v(15.54, -74.89) * mm, v(15.57, -75.53) * mm, v(15.43, -76.04) * mm]});
            skFitSpline(sketch, "E246", {"points": [v(15.43, -76.04) * mm, v(15.14, -77.06) * mm, v(14.45, -77.87) * mm, v(13.85, -77.87) * mm]});
            skFitSpline(sketch, "E247", {"points": [v(13.85, -77.87) * mm, v(13.06, -77.87) * mm, v(13.01, -78.27) * mm, v(13.7, -79) * mm]});
            skFitSpline(sketch, "E248", {"points": [v(13.7, -79) * mm, v(14.06, -79.37) * mm, v(14.38, -79.86) * mm, v(14.43, -80.1) * mm]});
            skFitSpline(sketch, "E249", {"points": [v(14.43, -80.1) * mm, v(14.5, -80.48) * mm, v(14.55, -80.47) * mm, v(15.03, -79.9) * mm]});
            skFitSpline(sketch, "E250", {"points": [v(15.03, -79.9) * mm, v(15.31, -79.57) * mm, v(16.02, -78.83) * mm, v(16.6, -78.28) * mm]});
            skFitSpline(sketch, "E251", {"points": [v(16.6, -78.28) * mm, v(17.64, -77.28) * mm, v(17.65, -77.26) * mm, v(17.4, -76.55) * mm]});
            skFitSpline(sketch, "E252", {"points": [v(17.4, -76.55) * mm, v(17.05, -75.6) * mm, v(17.07, -74.87) * mm, v(17.45, -74.37) * mm]});
            skFitSpline(sketch, "E253", {"points": [v(17.45, -74.37) * mm, v(17.62, -74.14) * mm, v(17.76, -73.7) * mm, v(17.76, -73.4) * mm]});
            skFitSpline(sketch, "E254", {"points": [v(17.76, -73.4) * mm, v(17.77, -72.89) * mm, v(17.86, -72.83) * mm, v(18.88, -72.7) * mm]});
            skFitSpline(sketch, "E255", {"points": [v(18.88, -72.7) * mm, v(19.5, -72.62) * mm, v(20.47, -72.3) * mm, v(21.04, -71.99) * mm]});
            skFitSpline(sketch, "E256", {"points": [v(21.04, -71.99) * mm, v(22.45, -71.22) * mm, v(23.22, -70.08) * mm, v(23.5, -68.35) * mm]});
            skFitSpline(sketch, "E257", {"points": [v(23.5, -68.35) * mm, v(23.9, -65.9) * mm, v(24.16, -65.2) * mm, v(25.1, -63.87) * mm]});
            skFitSpline(sketch, "E258", {"points": [v(25.1, -63.87) * mm, v(26.18, -62.33) * mm, v(26.35, -61.85) * mm, v(26.67, -59.46) * mm]});
            skFitSpline(sketch, "E259", {"points": [v(26.67, -59.46) * mm, v(26.98, -57.13) * mm, v(27.93, -54.18) * mm, v(28.89, -52.58) * mm]});
            skFitSpline(sketch, "E260", {"points": [v(28.89, -52.58) * mm, v(29.3, -51.88) * mm, v(30.25, -50.69) * mm, v(31, -49.93) * mm]});
            skFitSpline(sketch, "E261", {"points": [v(31, -49.93) * mm, v(33.26, -47.61) * mm, v(35.36, -45.01) * mm, v(35.9, -43.88) * mm]});
            skFitSpline(sketch, "E262", {"points": [v(35.9, -43.88) * mm, v(36.17, -43.28) * mm, v(36.49, -42.11) * mm, v(36.6, -41.27) * mm]});
            skFitSpline(sketch, "E263", {"points": [v(36.6, -41.27) * mm, v(36.81, -39.5) * mm, v(37.06, -39.06) * mm, v(38.37, -38.07) * mm]});
            skFitSpline(sketch, "E264", {"points": [v(38.37, -38.07) * mm, v(39.26, -37.4) * mm, v(40.2, -36.1) * mm, v(40.2, -35.57) * mm]});
            skFitSpline(sketch, "E265", {"points": [v(40.2, -35.57) * mm, v(40.2, -35.45) * mm, v(39.98, -35.11) * mm, v(39.7, -34.83) * mm]});
            skFitSpline(sketch, "E266", {"points": [v(39.7, -34.83) * mm, v(38.98, -34.12) * mm, v(38.86, -33.18) * mm, v(39.13, -30.68) * mm]});
            skFitSpline(sketch, "E267", {"points": [v(39.13, -30.68) * mm, v(39.26, -29.5) * mm, v(39.36, -26.93) * mm, v(39.36, -24.95) * mm]});
            skFitSpline(sketch, "E268", {"points": [v(39.36, -24.95) * mm, v(39.36, -21.87) * mm, v(39.3, -21.22) * mm, v(38.94, -20.3) * mm]});
            skFitSpline(sketch, "E269", {"points": [v(38.94, -20.3) * mm, v(38.39, -18.9) * mm, v(38.4, -18.51) * mm, v(39.04, -18) * mm]});
            skFitSpline(sketch, "E270", {"points": [v(39.04, -18) * mm, v(39.45, -17.69) * mm, v(39.57, -17.4) * mm, v(39.57, -16.76) * mm]});
            skFitSpline(sketch, "E271", {"points": [v(39.57, -16.76) * mm, v(39.57, -16.2) * mm, v(39.7, -15.8) * mm, v(39.97, -15.56) * mm]});
            skFitSpline(sketch, "E272", {"points": [v(39.97, -15.56) * mm, v(40.59, -15) * mm, v(40.32, -14.37) * mm, v(39.46, -14.37) * mm]});
            skFitSpline(sketch, "E273", {"points": [v(39.46, -14.37) * mm, v(38.38, -14.37) * mm, v(37.67, -13.4) * mm, v(37.67, -11.9) * mm]});
            skFitSpline(sketch, "E274", {"points": [v(37.67, -11.9) * mm, v(37.67, -10.72) * mm, v(37.93, -9.95) * mm, v(38.44, -9.65) * mm]});
            skFitSpline(sketch, "E275", {"points": [v(38.44, -9.65) * mm, v(39.04, -9.3) * mm, v(38.7, -8.02) * mm, v(38, -8.02) * mm]});
            skFitSpline(sketch, "E276", {"points": [v(38, -8.02) * mm, v(37.74, -8.02) * mm, v(37, -7.64) * mm, v(36.34, -7.18) * mm]});
            skFitSpline(sketch, "E277", {"points": [v(36.34, -7.18) * mm, v(35.18, -6.34) * mm, v(34.43, -6.12) * mm, v(34.18, -6.54) * mm]});
            skFitSpline(sketch, "E278", {"points": [v(34.18, -6.54) * mm, v(34.1, -6.66) * mm, v(33.87, -6.75) * mm, v(33.65, -6.75) * mm]});
            skFitSpline(sketch, "E279", {"points": [v(33.65, -6.75) * mm, v(33.07, -6.75) * mm, v(30.08, -5.09) * mm, v(29.83, -4.63) * mm]});
            skFitSpline(sketch, "E280", {"points": [v(29.83, -4.63) * mm, v(29.5, -4) * mm, v(29.6, -2.89) * mm, v(30.04, -2.22) * mm]});
            skFitSpline(sketch, "E281", {"points": [v(30.04, -2.22) * mm, v(30.4, -1.66) * mm, v(30.41, -1.54) * mm, v(30.14, -1.01) * mm]});
            skFitSpline(sketch, "E282", {"points": [v(30.14, -1.01) * mm, v(29.71, -0.19) * mm, v(29.76, 0.38) * mm, v(30.37, 1.68) * mm]});
            skFitSpline(sketch, "E283", {"points": [v(30.37, 1.68) * mm, v(30.96, 2.95) * mm, v(31, 3.5) * mm, v(30.65, 4.7) * mm]});
            skFitSpline(sketch, "E284", {"points": [v(30.65, 4.7) * mm, v(30.44, 5.4) * mm, v(30.46, 5.58) * mm, v(30.78, 5.93) * mm]});
            skFitSpline(sketch, "E285", {"points": [v(30.78, 5.93) * mm, v(31.13, 6.33) * mm, v(31.13, 6.4) * mm, v(30.68, 7.79) * mm]});
            skFitSpline(sketch, "E286", {"points": [v(30.68, 7.79) * mm, v(30.01, 9.8) * mm, v(29.64, 10.47) * mm, v(28.1, 12.43) * mm]});
            skFitSpline(sketch, "E287", {"points": [v(28.1, 12.43) * mm, v(27.35, 13.37) * mm, v(26.61, 14.44) * mm, v(26.46, 14.8) * mm]});
            skFitSpline(sketch, "E288", {"points": [v(26.46, 14.8) * mm, v(26, 15.95) * mm, v(26.28, 17.5) * mm, v(27.26, 19.16) * mm]});
            skFitSpline(sketch, "E289", {"points": [v(27.26, 19.16) * mm, v(28.4, 21.1) * mm, v(28.53, 21.7) * mm, v(27.93, 22.5) * mm]});
            skFitSpline(sketch, "E290", {"points": [v(27.93, 22.5) * mm, v(27.4, 23.23) * mm, v(27.46, 23.77) * mm, v(28.28, 25.17) * mm]});
            skFitSpline(sketch, "E291", {"points": [v(28.28, 25.17) * mm, v(28.94, 26.3) * mm, v(29.89, 26.9) * mm, v(31.02, 26.9) * mm]});
            skFitSpline(sketch, "E292", {"points": [v(31.02, 26.9) * mm, v(31.6, 26.9) * mm, v(32.1, 27.06) * mm, v(32.48, 27.36) * mm]});
            skFitSpline(sketch, "E293", {"points": [v(32.48, 27.36) * mm, v(33, 27.78) * mm, v(33.05, 27.91) * mm, v(32.96, 28.95) * mm]});
            skFitSpline(sketch, "E294", {"points": [v(32.96, 28.95) * mm, v(32.91, 29.57) * mm, v(32.82, 30.13) * mm, v(32.76, 30.19) * mm]});
            skFitSpline(sketch, "E295", {"points": [v(32.76, 30.19) * mm, v(32.7, 30.25) * mm, v(32.3, 30.15) * mm, v(31.89, 29.97) * mm]});
            skFitSpline(sketch, "E296", {"points": [v(31.89, 29.97) * mm, v(31.46, 29.8) * mm, v(31.06, 29.65) * mm, v(30.98, 29.65) * mm]});
            skFitSpline(sketch, "E297", {"points": [v(30.98, 29.65) * mm, v(30.9, 29.65) * mm, v(30.9, 30.37) * mm, v(30.97, 31.24) * mm]});
            skFitSpline(sketch, "E298", {"points": [v(30.97, 31.24) * mm, v(31.1, 32.73) * mm, v(31.07, 32.83) * mm, v(30.68, 32.83) * mm]});
            skFitSpline(sketch, "E299", {"points": [v(30.68, 32.83) * mm, v(30.45, 32.83) * mm, v(30.26, 32.97) * mm, v(30.26, 33.15) * mm]});
            skFitSpline(sketch, "E300", {"points": [v(30.26, 33.15) * mm, v(30.26, 33.32) * mm, v(30.16, 33.46) * mm, v(30.05, 33.46) * mm]});
            skFitSpline(sketch, "E301", {"points": [v(30.05, 33.46) * mm, v(29.69, 33.46) * mm, v(29.82, 34.44) * mm, v(30.23, 34.81) * mm]});
            skFitSpline(sketch, "E302", {"points": [v(30.23, 34.81) * mm, v(30.44, 35) * mm, v(31.16, 35.28) * mm, v(31.83, 35.42) * mm]});
            skFitSpline(sketch, "E303", {"points": [v(31.83, 35.42) * mm, v(32.85, 35.63) * mm, v(33.13, 35.62) * mm, v(33.6, 35.36) * mm]});
            skFitSpline(sketch, "E304", {"points": [v(33.6, 35.36) * mm, v(34.37, 34.93) * mm, v(34.48, 34.05) * mm, v(33.82, 33.73) * mm]});
            skFitSpline(sketch, "E305", {"points": [v(33.82, 33.73) * mm, v(33.34, 33.51) * mm, v(33.35, 33.5) * mm, v(34.15, 33.16) * mm]});
            skFitSpline(sketch, "E306", {"points": [v(34.15, 33.16) * mm, v(34.9, 32.83) * mm, v(34.99, 32.83) * mm, v(35.36, 33.17) * mm]});
            skFitSpline(sketch, "E307", {"points": [v(35.36, 33.17) * mm, v(35.58, 33.37) * mm, v(35.76, 33.64) * mm, v(35.76, 33.77) * mm]});
            skFitSpline(sketch, "E308", {"points": [v(35.76, 33.77) * mm, v(35.76, 33.9) * mm, v(36.1, 34.7) * mm, v(36.5, 35.56) * mm]});
            skFitSpline(sketch, "E309", {"points": [v(36.5, 35.56) * mm, v(37.29, 37.18) * mm, v(37.3, 37.75) * mm, v(36.61, 38.12) * mm]});
            skFitSpline(sketch, "E310", {"points": [v(36.61, 38.12) * mm, v(36.14, 38.38) * mm, v(35.55, 38.19) * mm, v(35.55, 37.78) * mm]});
            skFitSpline(sketch, "E311", {"points": [v(35.55, 37.78) * mm, v(35.55, 36.66) * mm, v(30.79, 39.12) * mm, v(30.36, 40.45) * mm]});
            skFitSpline(sketch, "E312", {"points": [v(30.36, 40.45) * mm, v(30.3, 40.68) * mm, v(30.34, 41.05) * mm, v(30.47, 41.29) * mm]});
            skFitSpline(sketch, "E313", {"points": [v(30.47, 41.29) * mm, v(30.77, 41.86) * mm, v(31.55, 41.83) * mm, v(33.01, 41.2) * mm]});
            skFitSpline(sketch, "E314", {"points": [v(33.01, 41.2) * mm, v(34.25, 40.67) * mm, v(34.4, 40.66) * mm, v(34.2, 41.18) * mm]});
            skFitSpline(sketch, "E315", {"points": [v(34.2, 41.18) * mm, v(34.13, 41.4) * mm, v(33.81, 41.5) * mm, v(33.34, 41.5) * mm]});
            skFitSpline(sketch, "E316", {"points": [v(33.34, 41.5) * mm, v(32.48, 41.5) * mm, v(32.37, 41.83) * mm, v(32.97, 42.57) * mm]});
            skFitSpline(sketch, "E317", {"points": [v(32.97, 42.57) * mm, v(33.3, 42.96) * mm, v(33.56, 43.04) * mm, v(34.54, 43.04) * mm]});
            skFitSpline(sketch, "E318", {"points": [v(34.54, 43.04) * mm, v(36.05, 43.02) * mm, v(36.12, 43.25) * mm, v(35.4, 45.67) * mm]});
            skFitSpline(sketch, "E319", {"points": [v(35.4, 45.67) * mm, v(34.98, 47.1) * mm, v(34.9, 47.7) * mm, v(35.01, 48.62) * mm]});
            skFitSpline(sketch, "E320", {"points": [v(35.01, 48.62) * mm, v(35.1, 49.37) * mm, v(35.26, 49.76) * mm, v(35.45, 49.76) * mm]});
            skFitSpline(sketch, "E321", {"points": [v(35.45, 49.76) * mm, v(35.79, 49.76) * mm, v(36.46, 48.04) * mm, v(36.81, 46.27) * mm]});
            skFitSpline(sketch, "E322", {"points": [v(36.81, 46.27) * mm, v(37.15, 44.53) * mm, v(37.45, 43.62) * mm, v(37.68, 43.62) * mm]});
            skFitSpline(sketch, "E323", {"points": [v(37.68, 43.62) * mm, v(37.8, 43.62) * mm, v(37.88, 43.84) * mm, v(37.88, 44.1) * mm]});
            skFitSpline(sketch, "E324", {"points": [v(37.88, 44.1) * mm, v(37.88, 44.74) * mm, v(36.88, 48.83) * mm, v(36.6, 49.36) * mm]});
            skFitSpline(sketch, "E325", {"points": [v(36.6, 49.36) * mm, v(36.47, 49.6) * mm, v(36.29, 50.3) * mm, v(36.19, 50.92) * mm]});
            skFitSpline(sketch, "E326", {"points": [v(36.19, 50.92) * mm, v(36.09, 51.54) * mm, v(35.8, 52.48) * mm, v(35.57, 53.01) * mm]});
            skFitSpline(sketch, "E327", {"points": [v(35.57, 53.01) * mm, v(35.31, 53.57) * mm, v(35.13, 54.41) * mm, v(35.13, 55.03) * mm]});
            skFitSpline(sketch, "E328", {"points": [v(35.13, 55.03) * mm, v(35.13, 56.37) * mm, v(34.52, 57.14) * mm, v(33.05, 57.66) * mm]});
            skFitSpline(sketch, "E329", {"points": [v(33.05, 57.66) * mm, v(31.97, 58.05) * mm, v(31.44, 58.5) * mm, v(31.02, 59.34) * mm]});
            skFitSpline(sketch, "E330", {"points": [v(31.02, 59.34) * mm, v(30.64, 60.08) * mm, v(29.4, 60.31) * mm, v(25.6, 60.34) * mm]});
            skFitSpline(sketch, "E331", {"points": [v(25.6, 60.34) * mm, v(21.36, 60.37) * mm, v(20.2, 60.66) * mm, v(19.62, 61.83) * mm]});
            skFitSpline(sketch, "E332", {"points": [v(19.62, 61.83) * mm, v(19.42, 62.24) * mm, v(19.25, 63.05) * mm, v(19.25, 63.63) * mm]});
            skFitSpline(sketch, "E333", {"points": [v(19.25, 63.63) * mm, v(19.24, 64.97) * mm, v(18.71, 66.14) * mm, v(17.39, 67.73) * mm]});
            skFitSpline(sketch, "E334", {"points": [v(17.39, 67.73) * mm, v(15.95, 69.45) * mm, v(15.56, 70.55) * mm, v(15.72, 72.4) * mm]});
            skFitSpline(sketch, "E335", {"points": [v(15.72, 72.4) * mm, v(15.89, 74.42) * mm, v(15.61, 75.26) * mm, v(14.57, 75.97) * mm]});
            skFitSpline(sketch, "E336", {"points": [v(14.57, 75.97) * mm, v(13.8, 76.48) * mm, v(12.94, 77.13) * mm, v(10.52, 78.96) * mm]});
            skFitSpline(sketch, "E337", {"points": [v(10.52, 78.96) * mm, v(9.93, 79.4) * mm, v(9.37, 79.6) * mm, v(8.4, 79.72) * mm]});
            skFitSpline(sketch, "E338", {"points": [v(8.4, 79.72) * mm, v(7.67, 79.8) * mm, v(6.83, 80.05) * mm, v(6.52, 80.27) * mm]});
            skFitSpline(sketch, "E339", {"points": [v(6.52, 80.27) * mm, v(5.73, 80.83) * mm, v(4.99, 80.76) * mm, v(4.18, 80.06) * mm]});
            skFitSpline(sketch, "E340", {"points": [v(4.18, 80.06) * mm, v(3.06, 79.09) * mm, v(2.62, 78.93) * mm, v(1.4, 79.08) * mm]});
            skFitSpline(sketch, "E341", {"points": [v(-1.23, 77.67) * mm, v(-2.35, 76.53) * mm, v(-2.88, 75.8) * mm, v(-3.2, 74.95) * mm]});
            skFitSpline(sketch, "E342", {"points": [v(-3.2, 74.95) * mm, v(-3.44, 74.31) * mm, v(-3.84, 73.58) * mm, v(-4.08, 73.32) * mm]});
            skFitSpline(sketch, "E343", {"points": [v(-4.08, 73.32) * mm, v(-4.6, 72.75) * mm, v(-5.86, 72.28) * mm, v(-7.31, 72.1) * mm]});
            skFitSpline(sketch, "E344", {"points": [v(-7.31, 72.1) * mm, v(-8.5, 71.94) * mm, v(-9.16, 71.58) * mm, v(-9.92, 70.68) * mm]});
            skFitSpline(sketch, "E345", {"points": [v(-9.92, 70.68) * mm, v(-10.62, 69.85) * mm, v(-11.46, 69.45) * mm, v(-12.51, 69.45) * mm]});
            skFitSpline(sketch, "E346", {"points": [v(-13.27, 67.07) * mm, v(-13.12, 64.4) * mm, v(-13.35, 63.34) * mm, v(-14.15, 63) * mm]});
            skFitSpline(sketch, "E347", {"points": [v(-14.15, 63) * mm, v(-14.41, 62.88) * mm, v(-14.68, 62.54) * mm, v(-14.74, 62.25) * mm]});
            skFitSpline(sketch, "E348", {"points": [v(-14.74, 62.25) * mm, v(-14.95, 61.27) * mm, v(-15.22, 60.8) * mm, v(-15.67, 60.66) * mm]});
            skFitSpline(sketch, "E349", {"points": [v(-15.67, 60.66) * mm, v(-16.3, 60.47) * mm, v(-17.15, 61.07) * mm, v(-17.15, 61.71) * mm]});
            skFitSpline(sketch, "E350", {"points": [v(-17.15, 61.71) * mm, v(-17.15, 62.4) * mm, v(-17.57, 62.62) * mm, v(-17.95, 62.12) * mm]});
            skFitSpline(sketch, "E351", {"points": [v(-17.95, 62.12) * mm, v(-18.25, 61.72) * mm, v(-18.24, 60.86) * mm, v(-17.87, 57.55) * mm]});
            skFitSpline(sketch, "E352", {"points": [v(-17.87, 57.55) * mm, v(-17.76, 56.53) * mm, v(-17.83, 56.11) * mm, v(-18.31, 54.9) * mm]});
            skFitSpline(sketch, "E353", {"points": [v(-18.43, 53.1) * mm, v(-18.09, 52.84) * mm, v(-18, 52.61) * mm, v(-18.12, 52.26) * mm]});
            skFitSpline(sketch, "E354", {"points": [v(-18.12, 52.26) * mm, v(-18.35, 51.5) * mm, v(-18.6, 51.29) * mm, v(-19.44, 51.14) * mm]});
            skFitSpline(sketch, "E355", {"points": [v(-19.44, 51.14) * mm, v(-20.16, 51.02) * mm, v(-20.25, 50.92) * mm, v(-20.59, 49.92) * mm]});
            skFitSpline(sketch, "E356", {"points": [v(-20.59, 49.92) * mm, v(-21.07, 48.49) * mm, v(-20.79, 47.82) * mm, v(-19.64, 47.63) * mm]});
            skFitSpline(sketch, "E357", {"points": [v(-19.64, 47.63) * mm, v(-18.7, 47.48) * mm, v(-18.1, 46.98) * mm, v(-17.9, 46.22) * mm]});
            skFitSpline(sketch, "E358", {"points": [v(-17.9, 46.22) * mm, v(-17.82, 45.92) * mm, v(-17.92, 44.77) * mm, v(-18.12, 43.68) * mm]});
            skFitSpline(sketch, "E359", {"points": [v(-18.12, 43.68) * mm, v(-18.44, 41.9) * mm, v(-18.54, 41.66) * mm, v(-19.03, 41.44) * mm]});
            skFitSpline(sketch, "E360", {"points": [v(-19.03, 41.44) * mm, v(-19.33, 41.3) * mm, v(-19.75, 41.02) * mm, v(-19.96, 40.82) * mm]});
            skFitSpline(sketch, "E361", {"points": [v(-19.96, 40.82) * mm, v(-20.16, 40.62) * mm, v(-20.6, 40.45) * mm, v(-20.94, 40.45) * mm]});
            skFitSpline(sketch, "E362", {"points": [v(-21.44, 41.8) * mm, v(-21.32, 43.27) * mm, v(-21.6, 44.43) * mm, v(-22.21, 44.98) * mm]});
            skFitSpline(sketch, "E363", {"points": [v(-22.21, 44.98) * mm, v(-22.54, 45.28) * mm, v(-22.7, 45.3) * mm, v(-23.16, 45.08) * mm]});
            skFitSpline(sketch, "E364", {"points": [v(-23.16, 45.08) * mm, v(-23.48, 44.93) * mm, v(-23.72, 44.65) * mm, v(-23.72, 44.41) * mm]});
            skFitSpline(sketch, "E365", {"points": [v(-23.72, 44.41) * mm, v(-23.72, 44.19) * mm, v(-24.06, 43.69) * mm, v(-24.47, 43.3) * mm]});
            skFitSpline(sketch, "E366", {"points": [v(-24.8, 41.05) * mm, v(-24.28, 39.2) * mm, v(-24.4, 38.43) * mm, v(-25.38, 37) * mm]});
            skFitSpline(sketch, "E367", {"points": [v(-25.38, 37) * mm, v(-26.38, 35.55) * mm, v(-26.52, 35.03) * mm, v(-26.15, 34.3) * mm]});
            skFitSpline(sketch, "E368", {"points": [v(-26.15, 34.3) * mm, v(-25.74, 33.52) * mm, v(-25.75, 32.64) * mm, v(-26.17, 31.34) * mm]});
            skFitSpline(sketch, "E369", {"points": [v(-26.17, 31.34) * mm, v(-26.5, 30.34) * mm, v(-26.5, 30.27) * mm, v(-26.05, 29.35) * mm]});
            skFitSpline(sketch, "E370", {"points": [v(-26.05, 29.35) * mm, v(-25.45, 28.12) * mm, v(-24.64, 27.64) * mm, v(-22.5, 27.27) * mm]});
            skFitSpline(sketch, "E371", {"points": [v(-22.5, 27.27) * mm, v(-21.03, 27.01) * mm, v(-20.71, 27.01) * mm, v(-20.51, 27.25) * mm]});
            skFitSpline(sketch, "E372", {"points": [v(-20.51, 27.25) * mm, v(-20.2, 27.62) * mm, v(-19.6, 27.62) * mm, v(-19.29, 27.24) * mm]});
            skFitSpline(sketch, "E373", {"points": [v(-19.29, 27.24) * mm, v(-18.74, 26.58) * mm, v(-18.77, 25.45) * mm, v(-19.37, 23.93) * mm]});
            skFitSpline(sketch, "E374", {"points": [v(-19.37, 23.93) * mm, v(-19.7, 23.08) * mm, v(-20.07, 22.46) * mm, v(-20.24, 22.46) * mm]});
            skFitSpline(sketch, "E375", {"points": [v(-20.24, 22.46) * mm, v(-20.4, 22.46) * mm, v(-20.54, 22.54) * mm, v(-20.54, 22.65) * mm]});
            skFitSpline(sketch, "E376", {"points": [v(-20.54, 22.65) * mm, v(-20.54, 23.08) * mm, v(-22.27, 25) * mm, v(-22.65, 25) * mm]});
            skFitSpline(sketch, "E377", {"points": [v(-22.65, 25) * mm, v(-23.23, 25) * mm, v(-23.72, 24.2) * mm, v(-23.72, 23.22) * mm]});
            skFitSpline(sketch, "E378", {"points": [v(-23.72, 23.22) * mm, v(-23.72, 22.72) * mm, v(-23.92, 22.04) * mm, v(-24.24, 21.5) * mm]});
            skFitSpline(sketch, "E379", {"points": [v(-24.24, 21.5) * mm, v(-24.66, 20.79) * mm, v(-24.75, 20.34) * mm, v(-24.74, 19.26) * mm]});
            skFitSpline(sketch, "E380", {"points": [v(-24.74, 19.26) * mm, v(-24.72, 18.51) * mm, v(-24.78, 17.69) * mm, v(-24.86, 17.43) * mm]});
            skFitSpline(sketch, "E381", {"points": [v(-24.86, 17.43) * mm, v(-25.08, 16.75) * mm, v(-24.82, 16.1) * mm, v(-24.33, 16.1) * mm]});
            skFitSpline(sketch, "E382", {"points": [v(-24.33, 16.1) * mm, v(-23.36, 16.1) * mm, v(-23.83, 14.55) * mm, v(-24.88, 14.3) * mm]});
            skFitSpline(sketch, "E383", {"points": [v(-24.88, 14.3) * mm, v(-25.3, 14.18) * mm, v(-25.36, 14.09) * mm, v(-25.2, 13.77) * mm]});
            skFitSpline(sketch, "E384", {"points": [v(-25.2, 13.77) * mm, v(-24.96, 13.34) * mm, v(-24.91, 12.23) * mm, v(-25.11, 12.03) * mm]});
            skFitSpline(sketch, "E385", {"points": [v(-25.11, 12.03) * mm, v(-25.18, 11.96) * mm, v(-25.46, 11.98) * mm, v(-25.73, 12.09) * mm]});
            skFitSpline(sketch, "E386", {"points": [v(-25.73, 12.09) * mm, v(-26.03, 12.2) * mm, v(-26.5, 12.18) * mm, v(-26.98, 12.04) * mm]});
            skFitSpline(sketch, "E387", {"points": [v(-26.98, 12.04) * mm, v(-28.78, 11.48) * mm, v(-28.79, 13.48) * mm, v(-26.99, 14.98) * mm]});
            skFitSpline(sketch, "E388", {"points": [v(-26.99, 14.98) * mm, v(-26.47, 15.42) * mm, v(-26.04, 15.92) * mm, v(-26.04, 16.09) * mm]});
            skFitSpline(sketch, "E389", {"points": [v(-26.04, 16.09) * mm, v(-26.04, 16.33) * mm, v(-26.1, 16.35) * mm, v(-26.3, 16.15) * mm]});
            skFitSpline(sketch, "E390", {"points": [v(-26.3, 16.15) * mm, v(-26.76, 15.69) * mm, v(-27.73, 15.86) * mm, v(-28.39, 16.52) * mm]});
            skFitSpline(sketch, "E391", {"points": [v(-28.39, 16.52) * mm, v(-28.98, 17.1) * mm, v(-29, 17.22) * mm, v(-29, 18.97) * mm]});
            skFitSpline(sketch, "E392", {"points": [v(-29, 18.97) * mm, v(-29, 20.63) * mm, v(-29.05, 20.82) * mm, v(-29.43, 20.91) * mm]});
            skFitSpline(sketch, "E393", {"points": [v(-29.43, 20.91) * mm, v(-30.19, 21.11) * mm, v(-29.94, 22.23) * mm, v(-28.69, 24.26) * mm]});
            skFitSpline(sketch, "E394", {"points": [v(-28.69, 24.26) * mm, v(-27.87, 25.58) * mm, v(-28, 27.33) * mm, v(-28.9, 27.33) * mm]});
            skFitSpline(sketch, "E395", {"points": [v(-28.9, 27.33) * mm, v(-29.17, 27.33) * mm, v(-29.7, 27.61) * mm, v(-30.07, 27.96) * mm]});
            skFitSpline(sketch, "E396", {"points": [v(-30.07, 27.96) * mm, v(-30.87, 28.71) * mm, v(-31.12, 28.76) * mm, v(-31.12, 28.14) * mm]});
            skFitSpline(sketch, "E397", {"points": [v(-31.12, 28.14) * mm, v(-31.12, 27.9) * mm, v(-30.7, 27.23) * mm, v(-30.17, 26.67) * mm]});
            skFitSpline(sketch, "E398", {"points": [v(-30.17, 26.67) * mm, v(-29.12, 25.55) * mm, v(-29.07, 25.4) * mm, v(-29.55, 24.9) * mm]});
            skFitSpline(sketch, "E399", {"points": [v(-29.55, 24.9) * mm, v(-30.1, 24.36) * mm, v(-30.96, 24.5) * mm, v(-31.6, 25.23) * mm]});
            skFitSpline(sketch, "E400", {"points": [v(-31.6, 25.23) * mm, v(-32.15, 25.85) * mm, v(-32.25, 25.88) * mm, v(-33.19, 25.74) * mm]});
            skFitSpline(sketch, "E401", {"points": [v(-33.19, 25.74) * mm, v(-34.37, 25.57) * mm, v(-35.26, 25.15) * mm, v(-35.43, 24.68) * mm]});
            skFitSpline(sketch, "E402", {"points": [v(-35.43, 24.68) * mm, v(-35.6, 24.23) * mm, v(-35.14, 24.08) * mm, v(-34.43, 24.35) * mm]});
            skFitSpline(sketch, "E403", {"points": [v(-34.43, 24.35) * mm, v(-34.1, 24.48) * mm, v(-33.54, 24.57) * mm, v(-33.15, 24.57) * mm]});
            skFitSpline(sketch, "E404", {"points": [v(-33.15, 24.57) * mm, v(-32.54, 24.57) * mm, v(-32.46, 24.5) * mm, v(-32.44, 24) * mm]});
            skFitSpline(sketch, "E405", {"points": [v(-32.44, 24) * mm, v(-32.43, 23.67) * mm, v(-32.27, 23.06) * mm, v(-32.1, 22.62) * mm]});
            skFitSpline(sketch, "E406", {"points": [v(-32.1, 22.62) * mm, v(-31.58, 21.42) * mm, v(-31.67, 20.28) * mm, v(-32.4, 18.86) * mm]});
            skFitSpline(sketch, "E407", {"points": [v(-32.4, 18.86) * mm, v(-33.14, 17.4) * mm, v(-33.17, 17.05) * mm, v(-32.63, 16.75) * mm]});
            skFitSpline(sketch, "E408", {"points": [v(-32.63, 16.75) * mm, v(-32.1, 16.47) * mm, v(-31.55, 14.82) * mm, v(-31.55, 13.54) * mm]});
            skFitSpline(sketch, "E409", {"points": [v(-31.55, 13.54) * mm, v(-31.55, 12.77) * mm, v(-31.45, 12.46) * mm, v(-31.11, 12.23) * mm]});
            skFitSpline(sketch, "E410", {"points": [v(-31.11, 12.23) * mm, v(-30.88, 12.06) * mm, v(-30.63, 11.6) * mm, v(-30.56, 11.18) * mm]});
            skFitSpline(sketch, "E411", {"points": [v(-30.56, 11.18) * mm, v(-30.46, 10.56) * mm, v(-30.52, 10.4) * mm, v(-30.91, 10.18) * mm]});
            skFitSpline(sketch, "E412", {"points": [v(-30.91, 10.18) * mm, v(-31.53, 9.85) * mm, v(-32.75, 10.1) * mm, v(-33.03, 10.6) * mm]});
            skFitSpline(sketch, "E413", {"points": [v(-33.03, 10.6) * mm, v(-33.14, 10.82) * mm, v(-33.25, 11.41) * mm, v(-33.26, 11.91) * mm]});
            skFitSpline(sketch, "E414", {"points": [v(-33.26, 11.91) * mm, v(-33.27, 12.53) * mm, v(-33.55, 13.4) * mm, v(-34.16, 14.63) * mm]});
            skFitSpline(sketch, "E415", {"points": [v(-34.16, 14.63) * mm, v(-34.97, 16.28) * mm, v(-35.1, 16.43) * mm, v(-35.72, 16.5) * mm]});
            skFitSpline(sketch, "E416", {"points": [v(-35.72, 16.5) * mm, v(-36.31, 16.55) * mm, v(-36.58, 16.38) * mm, v(-37.73, 15.23) * mm]});
            skFitSpline(sketch, "E417", {"points": [v(-37.73, 15.23) * mm, v(-38.93, 14.04) * mm, v(-39.01, 13.9) * mm, v(-38.59, 13.83) * mm]});
            skFitSpline(sketch, "E418", {"points": [v(-38.59, 13.83) * mm, v(-38.17, 13.76) * mm, v(-38.1, 13.62) * mm, v(-38.11, 12.76) * mm]});
            skFitSpline(sketch, "E419", {"points": [v(-38.11, 12.76) * mm, v(-38.12, 12.21) * mm, v(-38.4, 10.97) * mm, v(-38.75, 9.98) * mm]});
            skFitSpline(sketch, "E420", {"points": [v(-38.75, 9.98) * mm, v(-39.51, 7.8) * mm, v(-39.52, 7.37) * mm, v(-38.83, 5.2) * mm]});
            skFitSpline(sketch, "E421", {"points": [v(-38.83, 5.2) * mm, v(-38.38, 3.8) * mm, v(-38.3, 3.15) * mm, v(-38.32, 1.4) * mm]});
            skFitSpline(sketch, "E422", {"points": [v(-38.32, 1.4) * mm, v(-38.34, 0.23) * mm, v(-38.26, -1.1) * mm, v(-38.13, -1.57) * mm]});
            skFitSpline(sketch, "E423", {"points": [v(-38.13, -1.57) * mm, v(-37.77, -2.92) * mm, v(-37.86, -6.07) * mm, v(-38.34, -8.88) * mm]});
            skFitSpline(sketch, "E424", {"points": [v(-38.34, -8.88) * mm, v(-38.63, -10.58) * mm, v(-38.76, -12.12) * mm, v(-38.71, -13.3) * mm]});
            skFitSpline(sketch, "E425", {"points": [v(-38.71, -13.3) * mm, v(-38.65, -14.92) * mm, v(-38.56, -15.24) * mm, v(-37.96, -16.18) * mm]});
            skFitSpline(sketch, "E426", {"points": [v(-37.41, -20.41) * mm, v(-37.55, -24.06) * mm, v(-37.43, -24.65) * mm, v(-36.22, -26.18) * mm]});
            skFitSpline(sketch, "E427", {"points": [v(-36.22, -26.18) * mm, v(-34.5, -28.36) * mm, v(-33.66, -30.2) * mm, v(-33.66, -31.8) * mm]});
            skFitSpline(sketch, "E428", {"points": [v(-33.66, -31.8) * mm, v(-33.66, -32.5) * mm, v(-33.82, -32.8) * mm, v(-34.62, -33.66) * mm]});
            skFitSpline(sketch, "E429", {"points": [v(-34.62, -33.66) * mm, v(-35.46, -34.56) * mm, v(-35.57, -34.79) * mm, v(-35.57, -35.64) * mm]});
            skFitSpline(sketch, "E430", {"points": [v(-35.57, -35.64) * mm, v(-35.57, -36.85) * mm, v(-35.16, -37.86) * mm, v(-34.2, -38.96) * mm]});
            skFitSpline(sketch, "E431", {"points": [v(-34.2, -38.96) * mm, v(-33.8, -39.44) * mm, v(-33.28, -40.4) * mm, v(-33.04, -41.1) * mm]});
            skFitSpline(sketch, "E432", {"points": [v(-33.04, -41.1) * mm, v(-32.76, -41.93) * mm, v(-32.24, -42.8) * mm, v(-31.56, -43.59) * mm]});
            skFitSpline(sketch, "E433", {"points": [v(-31.56, -43.59) * mm, v(-29.64, -45.8) * mm, v(-29.61, -45.88) * mm, v(-29.6, -49.55) * mm]});
            skFitSpline(sketch, "E434", {"points": [v(-29.6, -49.55) * mm, v(-29.59, -51.33) * mm, v(-29.65, -53.1) * mm, v(-29.74, -53.47) * mm]});
            skFitSpline(sketch, "E435", {"points": [v(-29.74, -53.47) * mm, v(-29.87, -54.05) * mm, v(-29.78, -54.34) * mm, v(-29.2, -55.24) * mm]});
            skFitSpline(sketch, "E436", {"points": [v(-29.2, -55.24) * mm, v(-28.02, -57.1) * mm, v(-28.34, -58.63) * mm, v(-30.4, -60.92) * mm]});
            skFitSpline(sketch, "E437", {"points": [v(-30.9, -63.02) * mm, v(-30.62, -63.56) * mm, v(-29.54, -65.09) * mm, v(-28.5, -66.4) * mm]});
            skFitSpline(sketch, "E438", {"points": [v(-28.5, -66.4) * mm, v(-27.47, -67.73) * mm, v(-25.87, -70.02) * mm, v(-24.93, -71.5) * mm]});
            skFitSpline(sketch, "E439", {"points": [v(-24.93, -71.5) * mm, v(-21.66, -76.64) * mm, v(-20.53, -77.82) * mm, v(-18.3, -78.38) * mm]});
            skFitSpline(sketch, "E440", {"points": [v(-18.3, -78.38) * mm, v(-17.5, -78.58) * mm, v(-15.88, -79.13) * mm, v(-14.72, -79.6) * mm]});
            skFitSpline(sketch, "E441", {"points": [v(-14.72, -79.6) * mm, v(-13.56, -80.07) * mm, v(-12.22, -80.53) * mm, v(-11.76, -80.63) * mm]});
            skFitSpline(sketch, "E442", {"points": [v(-11.76, -80.63) * mm, v(-10.67, -80.86) * mm, v(-8.14, -80.7) * mm, v(-6.84, -80.3) * mm]});
            skFitSpline(sketch, "E443", {"points": [v(-34.5, 19.17) * mm, v(-34.65, 19.34) * mm, v(-35.11, 19.55) * mm, v(-35.54, 19.62) * mm]});
            skFitSpline(sketch, "E444", {"points": [v(-35.54, 19.62) * mm, v(-35.99, 19.7) * mm, v(-36.79, 20.15) * mm, v(-37.44, 20.68) * mm]});
            skFitSpline(sketch, "E445", {"points": [v(-37.44, 20.68) * mm, v(-38.07, 21.2) * mm, v(-38.96, 21.72) * mm, v(-39.42, 21.86) * mm]});
            skFitSpline(sketch, "E446", {"points": [v(-39.42, 21.86) * mm, v(-39.89, 22) * mm, v(-40.41, 22.34) * mm, v(-40.6, 22.6) * mm]});
            skFitSpline(sketch, "E447", {"points": [v(-40.6, 22.6) * mm, v(-40.88, 23.06) * mm, v(-40.88, 23.2) * mm, v(-40.52, 24.1) * mm]});
            skFitSpline(sketch, "E448", {"points": [v(-40.52, 24.1) * mm, v(-39.98, 25.46) * mm, v(-39.97, 28.27) * mm, v(-40.5, 29.07) * mm]});
            skFitSpline(sketch, "E449", {"points": [v(-40.5, 29.07) * mm, v(-40.94, 29.76) * mm, v(-40.96, 30.33) * mm, v(-40.55, 31.12) * mm]});
            skFitSpline(sketch, "E450", {"points": [v(-40.55, 31.12) * mm, v(-40.35, 31.5) * mm, v(-40.29, 32) * mm, v(-40.37, 32.52) * mm]});
            skFitSpline(sketch, "E451", {"points": [v(-40.37, 32.52) * mm, v(-40.49, 33.2) * mm, v(-40.43, 33.39) * mm, v(-39.97, 33.76) * mm]});
            skFitSpline(sketch, "E452", {"points": [v(-39.97, 33.76) * mm, v(-39.45, 34.2) * mm, v(-38.12, 36.16) * mm, v(-37.84, 36.9) * mm]});
            skFitSpline(sketch, "E453", {"points": [v(-37.84, 36.9) * mm, v(-37.74, 37.17) * mm, v(-37.47, 37.27) * mm, v(-36.87, 37.27) * mm]});
            skFitSpline(sketch, "E454", {"points": [v(-36.87, 37.27) * mm, v(-36.4, 37.27) * mm, v(-35.93, 37.4) * mm, v(-35.78, 37.6) * mm]});
            skFitSpline(sketch, "E455", {"points": [v(-35.78, 37.6) * mm, v(-35.64, 37.77) * mm, v(-35.2, 37.9) * mm, v(-34.82, 37.9) * mm]});
            skFitSpline(sketch, "E456", {"points": [v(-34.82, 37.9) * mm, v(-34.13, 37.9) * mm, v(-34.12, 37.9) * mm, v(-34.23, 37.12) * mm]});
            skFitSpline(sketch, "E457", {"points": [v(-34.23, 37.12) * mm, v(-34.47, 35.46) * mm, v(-34.75, 34.75) * mm, v(-35.37, 34.23) * mm]});
            skFitSpline(sketch, "E458", {"points": [v(-35.37, 34.23) * mm, v(-35.99, 33.7) * mm, v(-36, 33.67) * mm, v(-35.67, 33.16) * mm]});
            skFitSpline(sketch, "E459", {"points": [v(-35.67, 33.16) * mm, v(-34.87, 31.95) * mm, v(-36.1, 31.14) * mm, v(-37.5, 31.95) * mm]});
            skFitSpline(sketch, "E460", {"points": [v(-37.5, 31.95) * mm, v(-37.94, 32.2) * mm, v(-38.35, 32.4) * mm, v(-38.4, 32.4) * mm]});
            skFitSpline(sketch, "E461", {"points": [v(-38.4, 32.4) * mm, v(-38.63, 32.4) * mm, v(-38.23, 31.65) * mm, v(-37.44, 30.52) * mm]});
            skFitSpline(sketch, "E462", {"points": [v(-37.44, 30.52) * mm, v(-36.44, 29.1) * mm, v(-36.35, 28.09) * mm, v(-37.16, 27.33) * mm]});
            skFitSpline(sketch, "E463", {"points": [v(-37.16, 27.33) * mm, v(-37.75, 26.77) * mm, v(-37.88, 25.84) * mm, v(-37.36, 25.84) * mm]});
            skFitSpline(sketch, "E464", {"points": [v(-37.36, 25.84) * mm, v(-37.12, 25.84) * mm, v(-37.08, 25.7) * mm, v(-37.18, 25.26) * mm]});
            skFitSpline(sketch, "E465", {"points": [v(-37.18, 25.26) * mm, v(-37.37, 24.47) * mm, v(-37.66, 23.94) * mm, v(-37.9, 23.94) * mm]});
            skFitSpline(sketch, "E466", {"points": [v(-37.9, 23.94) * mm, v(-38.25, 23.94) * mm, v(-38.13, 23.18) * mm, v(-37.73, 22.82) * mm]});
            skFitSpline(sketch, "E467", {"points": [v(-37.73, 22.82) * mm, v(-37.52, 22.63) * mm, v(-36.88, 22.27) * mm, v(-36.3, 22.02) * mm]});
            skFitSpline(sketch, "E468", {"points": [v(-36.3, 22.02) * mm, v(-33.61, 20.87) * mm, v(-33.45, 20.76) * mm, v(-33.45, 20.13) * mm]});
            skFitSpline(sketch, "E469", {"points": [v(-33.45, 20.13) * mm, v(-33.45, 18.94) * mm, v(-33.94, 18.5) * mm, v(-34.5, 19.17) * mm]});
            skFitSpline(sketch, "E470", {"points": [v(-33.88, 20.11) * mm, v(-33.88, 20.2) * mm, v(-34.7, 20.65) * mm, v(-35.7, 21.1) * mm]});
            skFitSpline(sketch, "E471", {"points": [v(-35.7, 21.1) * mm, v(-38.2, 22.21) * mm, v(-38.53, 22.5) * mm, v(-38.53, 23.53) * mm]});
            skFitSpline(sketch, "E472", {"points": [v(-38.53, 23.53) * mm, v(-38.53, 23.99) * mm, v(-38.45, 24.36) * mm, v(-38.35, 24.36) * mm]});
            skFitSpline(sketch, "E473", {"points": [v(-38.35, 24.36) * mm, v(-38.26, 24.36) * mm, v(-38.08, 24.58) * mm, v(-37.96, 24.84) * mm]});
            skFitSpline(sketch, "E474", {"points": [v(-37.96, 24.84) * mm, v(-37.8, 25.2) * mm, v(-37.81, 25.39) * mm, v(-38.03, 25.6) * mm]});
            skFitSpline(sketch, "E475", {"points": [v(-38.03, 25.6) * mm, v(-38.5, 26.03) * mm, v(-38.36, 26.84) * mm, v(-37.67, 27.63) * mm]});
            skFitSpline(sketch, "E476", {"points": [v(-37.67, 27.63) * mm, v(-36.9, 28.51) * mm, v(-36.94, 28.8) * mm, v(-38.14, 30.48) * mm]});
            skFitSpline(sketch, "E477", {"points": [v(-38.14, 30.48) * mm, v(-38.63, 31.17) * mm, v(-38.96, 31.87) * mm, v(-38.96, 32.23) * mm]});
            skFitSpline(sketch, "E478", {"points": [v(-38.96, 32.23) * mm, v(-38.96, 32.75) * mm, v(-38.87, 32.83) * mm, v(-38.36, 32.83) * mm]});
            skFitSpline(sketch, "E479", {"points": [v(-38.36, 32.83) * mm, v(-38.03, 32.83) * mm, v(-37.58, 32.69) * mm, v(-37.36, 32.52) * mm]});
            skFitSpline(sketch, "E480", {"points": [v(-37.36, 32.52) * mm, v(-36.98, 32.23) * mm, v(-36, 32.07) * mm, v(-36, 32.3) * mm]});
            skFitSpline(sketch, "E481", {"points": [v(-36, 32.3) * mm, v(-36, 32.35) * mm, v(-36.15, 32.73) * mm, v(-36.35, 33.14) * mm]});
            skFitSpline(sketch, "E482", {"points": [v(-35.92, 34.57) * mm, v(-35.27, 35.14) * mm, v(-35.1, 35.46) * mm, v(-34.96, 36.38) * mm]});
            skFitSpline(sketch, "E483", {"points": [v(-34.96, 36.38) * mm, v(-34.86, 36.99) * mm, v(-34.82, 37.49) * mm, v(-34.87, 37.49) * mm]});
            skFitSpline(sketch, "E484", {"points": [v(-34.87, 37.49) * mm, v(-34.91, 37.49) * mm, v(-35.23, 37.28) * mm, v(-35.56, 37.04) * mm]});
            skFitSpline(sketch, "E485", {"points": [v(-35.56, 37.04) * mm, v(-35.96, 36.74) * mm, v(-36.36, 36.62) * mm, v(-36.72, 36.69) * mm]});
            skFitSpline(sketch, "E486", {"points": [v(-36.72, 36.69) * mm, v(-37.02, 36.75) * mm, v(-37.26, 36.72) * mm, v(-37.26, 36.64) * mm]});
            skFitSpline(sketch, "E487", {"points": [v(-37.26, 36.64) * mm, v(-37.26, 36.35) * mm, v(-39.4, 33.25) * mm, v(-39.6, 33.25) * mm]});
            skFitSpline(sketch, "E488", {"points": [v(-39.6, 33.25) * mm, v(-39.71, 33.25) * mm, v(-39.8, 32.75) * mm, v(-39.8, 32.14) * mm]});
            skFitSpline(sketch, "E489", {"points": [v(-39.8, 32.14) * mm, v(-39.81, 31.5) * mm, v(-39.95, 30.86) * mm, v(-40.13, 30.62) * mm]});
            skFitSpline(sketch, "E490", {"points": [v(-40.13, 30.62) * mm, v(-40.4, 30.26) * mm, v(-40.4, 30.15) * mm, v(-40.08, 29.67) * mm]});
            skFitSpline(sketch, "E491", {"points": [v(-40.08, 29.67) * mm, v(-39.54, 28.86) * mm, v(-39.43, 25.58) * mm, v(-39.9, 24.18) * mm]});
            skFitSpline(sketch, "E492", {"points": [v(-39.9, 24.18) * mm, v(-40.1, 23.59) * mm, v(-40.2, 23.02) * mm, v(-40.14, 22.92) * mm]});
            skFitSpline(sketch, "E493", {"points": [v(-40.14, 22.92) * mm, v(-40.08, 22.82) * mm, v(-39.57, 22.56) * mm, v(-39.02, 22.35) * mm]});
            skFitSpline(sketch, "E494", {"points": [v(-39.02, 22.35) * mm, v(-38.46, 22.15) * mm, v(-37.5, 21.56) * mm, v(-36.87, 21.05) * mm]});
            skFitSpline(sketch, "E495", {"points": [v(-36.87, 21.05) * mm, v(-36.12, 20.45) * mm, v(-35.53, 20.13) * mm, v(-35.13, 20.13) * mm]});
            skFitSpline(sketch, "E496", {"points": [v(-35.13, 20.13) * mm, v(-34.8, 20.13) * mm, v(-34.48, 20.03) * mm, v(-34.4, 19.91) * mm]});
            skFitSpline(sketch, "E497", {"points": [v(-34.4, 19.91) * mm, v(-34.26, 19.68) * mm, v(-33.88, 19.83) * mm, v(-33.88, 20.11) * mm]});
            skFitSpline(sketch, "E498", {"points": [v(-35.84, 27.25) * mm, v(-35.9, 27.35) * mm, v(-36.01, 27.96) * mm, v(-36.1, 28.6) * mm]});
            skFitSpline(sketch, "E499", {"points": [v(-36.1, 28.6) * mm, v(-36.27, 30.1) * mm, v(-35.9, 30.72) * mm, v(-35.07, 30.34) * mm]});
            skFitSpline(sketch, "E500", {"points": [v(-35.07, 30.34) * mm, v(-34.7, 30.18) * mm, v(-34.56, 29.98) * mm, v(-34.64, 29.77) * mm]});
            skFitSpline(sketch, "E501", {"points": [v(-34.64, 29.77) * mm, v(-34.74, 29.52) * mm, v(-34.61, 29.44) * mm, v(-34.1, 29.44) * mm]});
            skFitSpline(sketch, "E502", {"points": [v(-34.1, 29.44) * mm, v(-33.14, 29.44) * mm, v(-32.6, 29.1) * mm, v(-32.6, 28.48) * mm]});
            skFitSpline(sketch, "E503", {"points": [v(-32.6, 28.48) * mm, v(-32.6, 28.2) * mm, v(-32.71, 27.96) * mm, v(-32.85, 27.96) * mm]});
            skFitSpline(sketch, "E504", {"points": [v(-32.85, 27.96) * mm, v(-32.98, 27.96) * mm, v(-33.2, 27.8) * mm, v(-33.34, 27.62) * mm]});
            skFitSpline(sketch, "E505", {"points": [v(-33.34, 27.62) * mm, v(-33.62, 27.24) * mm, v(-35.65, 26.94) * mm, v(-35.84, 27.25) * mm]});
            skFitSpline(sketch, "E506", {"points": [v(-33.88, 28.07) * mm, v(-33.88, 28.24) * mm, v(-33.73, 28.38) * mm, v(-33.56, 28.38) * mm]});
            skFitSpline(sketch, "E507", {"points": [v(-33.56, 28.38) * mm, v(-33.38, 28.38) * mm, v(-33.24, 28.48) * mm, v(-33.24, 28.6) * mm]});
            skFitSpline(sketch, "E508", {"points": [v(-33.24, 28.6) * mm, v(-33.24, 28.71) * mm, v(-33.73, 28.8) * mm, v(-34.32, 28.8) * mm]});
            skFitSpline(sketch, "E509", {"points": [v(-34.32, 28.8) * mm, v(-35.4, 28.8) * mm, v(-35.4, 28.81) * mm, v(-35.31, 29.43) * mm]});
            skFitSpline(sketch, "E510", {"points": [v(-35.31, 29.43) * mm, v(-35.26, 29.77) * mm, v(-35.3, 30) * mm, v(-35.4, 29.95) * mm]});
            skFitSpline(sketch, "E511", {"points": [v(-35.4, 29.95) * mm, v(-35.6, 29.82) * mm, v(-35.62, 28.91) * mm, v(-35.44, 28.23) * mm]});
            skFitSpline(sketch, "E512", {"points": [v(-35.44, 28.23) * mm, v(-35.33, 27.85) * mm, v(-35.16, 27.75) * mm, v(-34.6, 27.75) * mm]});
            skFitSpline(sketch, "E513", {"points": [v(-34.6, 27.75) * mm, v(-34.1, 27.75) * mm, v(-33.88, 27.85) * mm, v(-33.88, 28.07) * mm]});
            skFitSpline(sketch, "E514", {"points": [v(-34.5, 30.49) * mm, v(-34.87, 31.18) * mm, v(-34.75, 31.97) * mm, v(-34.2, 32.53) * mm]});
            skFitSpline(sketch, "E515", {"points": [v(-34.2, 32.53) * mm, v(-33.9, 32.82) * mm, v(-33.66, 33.2) * mm, v(-33.66, 33.37) * mm]});
            skFitSpline(sketch, "E516", {"points": [v(-33.66, 33.37) * mm, v(-33.66, 33.54) * mm, v(-33.57, 33.68) * mm, v(-33.45, 33.68) * mm]});
            skFitSpline(sketch, "E517", {"points": [v(-33.45, 33.68) * mm, v(-33.34, 33.68) * mm, v(-33.24, 33.6) * mm, v(-33.24, 33.51) * mm]});
            skFitSpline(sketch, "E518", {"points": [v(-33.24, 33.51) * mm, v(-33.24, 33.42) * mm, v(-32.95, 33.24) * mm, v(-32.6, 33.1) * mm]});
            skFitSpline(sketch, "E519", {"points": [v(-32.6, 33.1) * mm, v(-31.72, 32.77) * mm, v(-31.8, 32.27) * mm, v(-32.94, 31.08) * mm]});
            skFitSpline(sketch, "E520", {"points": [v(-32.94, 31.08) * mm, v(-34, 29.96) * mm, v(-34.19, 29.9) * mm, v(-34.5, 30.49) * mm]});
            skFitSpline(sketch, "E521", {"points": [v(-32.6, 32.45) * mm, v(-32.6, 32.54) * mm, v(-32.75, 32.62) * mm, v(-32.92, 32.62) * mm]});
            skFitSpline(sketch, "E522", {"points": [v(-32.92, 32.62) * mm, v(-33.1, 32.62) * mm, v(-33.24, 32.53) * mm, v(-33.24, 32.43) * mm]});
            skFitSpline(sketch, "E523", {"points": [v(-33.24, 32.43) * mm, v(-33.24, 32.33) * mm, v(-33.43, 32.2) * mm, v(-33.66, 32.13) * mm]});
            skFitSpline(sketch, "E524", {"points": [v(-33.66, 32.13) * mm, v(-33.96, 32.06) * mm, v(-34.09, 31.84) * mm, v(-34.09, 31.43) * mm]});
            skFitSpline(sketch, "E525", {"points": [v(-33.35, 31.56) * mm, v(-32.94, 31.95) * mm, v(-32.6, 32.35) * mm, v(-32.6, 32.45) * mm]});
            skSolve(sketch);
        }
        {
            var Q0;
            Q0=makeQuery(id+"F0.imprint","IMPRINT",FACE,{"disambiguationData":[TD([[makeQuery(id+"F0.imprint","IMPRINT",EDGE,{"derivedFrom":sQuery(id+"F0.wireOp",EDGE,"E12")}),1.0]])]});
            var Q1;
            Q1=makeQuery(id+"F0.imprint","IMPRINT",FACE,{"disambiguationData":[TD([[makeQuery(id+"F0.imprint","IMPRINT",EDGE,{"derivedFrom":sQuery(id+"F0.wireOp",EDGE,"E26")}),1.0]])]});
            var Q2;
            Q2=makeQuery(id+"F0.imprint","IMPRINT",FACE,{"disambiguationData":[TD([[makeQuery(id+"F0.imprint","IMPRINT",EDGE,{"derivedFrom":sQuery(id+"F0.wireOp",EDGE,"E506")}),1.0]])]});
            var Q3;
            Q3=makeQuery(id+"F0.imprint","IMPRINT",FACE,{"disambiguationData":[TD([[makeQuery(id+"F0.imprint","IMPRINT",EDGE,{"derivedFrom":sQuery(id+"F0.wireOp",EDGE,"E28")}),1.0]])]});
            extrude(context, id + "F1", {"entities" : qUnion([Q0, Q1, Q2, Q3]), "depth" : 3 * mm, "offsetDistance" : 25 * mm});
        }
        {
            var Q0;
            Q0=makeQuery(id+"F1.opExtrude","CAP_FACE",FACE,{"disambiguationData":[OSD([sQuery(id+"F0.wireOp",EDGE,"E12"),sQuery(id+"F0.wireOp",EDGE,"E13"),sQuery(id+"F0.wireOp",EDGE,"E14"),sQuery(id+"F0.wireOp",EDGE,"E15"),sQuery(id+"F0.wireOp",EDGE,"E16"),sQuery(id+"F0.wireOp",EDGE,"E17"),sQuery(id+"F0.wireOp",EDGE,"E18"),sQuery(id+"F0.wireOp",EDGE,"E19"),sQuery(id+"F0.wireOp",EDGE,"E20"),sQuery(id+"F0.wireOp",EDGE,"E21"),sQuery(id+"F0.wireOp",EDGE,"E22"),sQuery(id+"F0.wireOp",EDGE,"E23"),sQuery(id+"F0.wireOp",EDGE,"E24"),sQuery(id+"F0.wireOp",EDGE,"E25"),sQuery(id+"F0.wireOp",EDGE,"E233"),sQuery(id+"F0.wireOp",EDGE,"E234"),sQuery(id+"F0.wireOp",EDGE,"E235"),sQuery(id+"F0.wireOp",EDGE,"E236"),sQuery(id+"F0.wireOp",EDGE,"E237"),sQuery(id+"F0.wireOp",EDGE,"E238"),sQuery(id+"F0.wireOp",EDGE,"E239"),sQuery(id+"F0.wireOp",EDGE,"E240"),sQuery(id+"F0.wireOp",EDGE,"E241"),sQuery(id+"F0.wireOp",EDGE,"E242"),sQuery(id+"F0.wireOp",EDGE,"E243"),sQuery(id+"F0.wireOp",EDGE,"E244"),sQuery(id+"F0.wireOp",EDGE,"E245"),sQuery(id+"F0.wireOp",EDGE,"E246"),sQuery(id+"F0.wireOp",EDGE,"E247"),sQuery(id+"F0.wireOp",EDGE,"E248"),sQuery(id+"F0.wireOp",EDGE,"E249"),sQuery(id+"F0.wireOp",EDGE,"E250"),sQuery(id+"F0.wireOp",EDGE,"E251"),sQuery(id+"F0.wireOp",EDGE,"E252"),sQuery(id+"F0.wireOp",EDGE,"E253"),sQuery(id+"F0.wireOp",EDGE,"E254"),sQuery(id+"F0.wireOp",EDGE,"E255"),sQuery(id+"F0.wireOp",EDGE,"E256"),sQuery(id+"F0.wireOp",EDGE,"E257"),sQuery(id+"F0.wireOp",EDGE,"E258"),sQuery(id+"F0.wireOp",EDGE,"E259"),sQuery(id+"F0.wireOp",EDGE,"E260"),sQuery(id+"F0.wireOp",EDGE,"E261"),sQuery(id+"F0.wireOp",EDGE,"E262"),sQuery(id+"F0.wireOp",EDGE,"E263"),sQuery(id+"F0.wireOp",EDGE,"E264"),sQuery(id+"F0.wireOp",EDGE,"E265"),sQuery(id+"F0.wireOp",EDGE,"E266"),sQuery(id+"F0.wireOp",EDGE,"E267"),sQuery(id+"F0.wireOp",EDGE,"E268"),sQuery(id+"F0.wireOp",EDGE,"E269"),sQuery(id+"F0.wireOp",EDGE,"E270"),sQuery(id+"F0.wireOp",EDGE,"E271"),sQuery(id+"F0.wireOp",EDGE,"E272"),sQuery(id+"F0.wireOp",EDGE,"E273"),sQuery(id+"F0.wireOp",EDGE,"E274"),sQuery(id+"F0.wireOp",EDGE,"E275"),sQuery(id+"F0.wireOp",EDGE,"E276"),sQuery(id+"F0.wireOp",EDGE,"E277"),sQuery(id+"F0.wireOp",EDGE,"E278"),sQuery(id+"F0.wireOp",EDGE,"E279"),sQuery(id+"F0.wireOp",EDGE,"E280"),sQuery(id+"F0.wireOp",EDGE,"E281"),sQuery(id+"F0.wireOp",EDGE,"E282"),sQuery(id+"F0.wireOp",EDGE,"E283"),sQuery(id+"F0.wireOp",EDGE,"E284"),sQuery(id+"F0.wireOp",EDGE,"E285"),sQuery(id+"F0.wireOp",EDGE,"E286"),sQuery(id+"F0.wireOp",EDGE,"E287"),sQuery(id+"F0.wireOp",EDGE,"E288"),sQuery(id+"F0.wireOp",EDGE,"E289"),sQuery(id+"F0.wireOp",EDGE,"E290"),sQuery(id+"F0.wireOp",EDGE,"E291"),sQuery(id+"F0.wireOp",EDGE,"E292"),sQuery(id+"F0.wireOp",EDGE,"E293"),sQuery(id+"F0.wireOp",EDGE,"E294"),sQuery(id+"F0.wireOp",EDGE,"E295"),sQuery(id+"F0.wireOp",EDGE,"E296"),sQuery(id+"F0.wireOp",EDGE,"E297"),sQuery(id+"F0.wireOp",EDGE,"E298"),sQuery(id+"F0.wireOp",EDGE,"E299"),sQuery(id+"F0.wireOp",EDGE,"E300"),sQuery(id+"F0.wireOp",EDGE,"E301"),sQuery(id+"F0.wireOp",EDGE,"E302"),sQuery(id+"F0.wireOp",EDGE,"E303"),sQuery(id+"F0.wireOp",EDGE,"E304"),sQuery(id+"F0.wireOp",EDGE,"E305"),sQuery(id+"F0.wireOp",EDGE,"E306"),sQuery(id+"F0.wireOp",EDGE,"E307"),sQuery(id+"F0.wireOp",EDGE,"E308"),sQuery(id+"F0.wireOp",EDGE,"E309"),sQuery(id+"F0.wireOp",EDGE,"E310"),sQuery(id+"F0.wireOp",EDGE,"E311"),sQuery(id+"F0.wireOp",EDGE,"E312"),sQuery(id+"F0.wireOp",EDGE,"E313"),sQuery(id+"F0.wireOp",EDGE,"E314"),sQuery(id+"F0.wireOp",EDGE,"E315"),sQuery(id+"F0.wireOp",EDGE,"E316"),sQuery(id+"F0.wireOp",EDGE,"E317"),sQuery(id+"F0.wireOp",EDGE,"E318"),sQuery(id+"F0.wireOp",EDGE,"E319"),sQuery(id+"F0.wireOp",EDGE,"E320"),sQuery(id+"F0.wireOp",EDGE,"E321"),sQuery(id+"F0.wireOp",EDGE,"E322"),sQuery(id+"F0.wireOp",EDGE,"E323"),sQuery(id+"F0.wireOp",EDGE,"E324"),sQuery(id+"F0.wireOp",EDGE,"E325"),sQuery(id+"F0.wireOp",EDGE,"E326"),sQuery(id+"F0.wireOp",EDGE,"E327"),sQuery(id+"F0.wireOp",EDGE,"E328"),sQuery(id+"F0.wireOp",EDGE,"E329"),sQuery(id+"F0.wireOp",EDGE,"E330"),sQuery(id+"F0.wireOp",EDGE,"E331"),sQuery(id+"F0.wireOp",EDGE,"E332"),sQuery(id+"F0.wireOp",EDGE,"E333"),sQuery(id+"F0.wireOp",EDGE,"E334"),sQuery(id+"F0.wireOp",EDGE,"E335"),sQuery(id+"F0.wireOp",EDGE,"E336"),sQuery(id+"F0.wireOp",EDGE,"E337"),sQuery(id+"F0.wireOp",EDGE,"E338"),sQuery(id+"F0.wireOp",EDGE,"E339"),sQuery(id+"F0.wireOp",EDGE,"E340"),sQuery(id+"F0.wireOp",EDGE,"E341"),sQuery(id+"F0.wireOp",EDGE,"E342"),sQuery(id+"F0.wireOp",EDGE,"E343"),sQuery(id+"F0.wireOp",EDGE,"E344"),sQuery(id+"F0.wireOp",EDGE,"E345"),sQuery(id+"F0.wireOp",EDGE,"E346"),sQuery(id+"F0.wireOp",EDGE,"E347"),sQuery(id+"F0.wireOp",EDGE,"E348"),sQuery(id+"F0.wireOp",EDGE,"E349"),sQuery(id+"F0.wireOp",EDGE,"E350"),sQuery(id+"F0.wireOp",EDGE,"E351"),sQuery(id+"F0.wireOp",EDGE,"E352"),sQuery(id+"F0.wireOp",EDGE,"E353"),sQuery(id+"F0.wireOp",EDGE,"E354"),sQuery(id+"F0.wireOp",EDGE,"E355"),sQuery(id+"F0.wireOp",EDGE,"E356"),sQuery(id+"F0.wireOp",EDGE,"E357"),sQuery(id+"F0.wireOp",EDGE,"E358"),sQuery(id+"F0.wireOp",EDGE,"E359"),sQuery(id+"F0.wireOp",EDGE,"E360"),sQuery(id+"F0.wireOp",EDGE,"E361"),sQuery(id+"F0.wireOp",EDGE,"E362"),sQuery(id+"F0.wireOp",EDGE,"E363"),sQuery(id+"F0.wireOp",EDGE,"E364"),sQuery(id+"F0.wireOp",EDGE,"E365"),sQuery(id+"F0.wireOp",EDGE,"E366"),sQuery(id+"F0.wireOp",EDGE,"E367"),sQuery(id+"F0.wireOp",EDGE,"E368"),sQuery(id+"F0.wireOp",EDGE,"E369"),sQuery(id+"F0.wireOp",EDGE,"E370"),sQuery(id+"F0.wireOp",EDGE,"E371"),sQuery(id+"F0.wireOp",EDGE,"E372"),sQuery(id+"F0.wireOp",EDGE,"E373"),sQuery(id+"F0.wireOp",EDGE,"E374"),sQuery(id+"F0.wireOp",EDGE,"E375"),sQuery(id+"F0.wireOp",EDGE,"E376"),sQuery(id+"F0.wireOp",EDGE,"E377"),sQuery(id+"F0.wireOp",EDGE,"E378"),sQuery(id+"F0.wireOp",EDGE,"E379"),sQuery(id+"F0.wireOp",EDGE,"E380"),sQuery(id+"F0.wireOp",EDGE,"E381"),sQuery(id+"F0.wireOp",EDGE,"E382"),sQuery(id+"F0.wireOp",EDGE,"E383"),sQuery(id+"F0.wireOp",EDGE,"E384"),sQuery(id+"F0.wireOp",EDGE,"E385"),sQuery(id+"F0.wireOp",EDGE,"E386"),sQuery(id+"F0.wireOp",EDGE,"E387"),sQuery(id+"F0.wireOp",EDGE,"E388"),sQuery(id+"F0.wireOp",EDGE,"E389"),sQuery(id+"F0.wireOp",EDGE,"E390"),sQuery(id+"F0.wireOp",EDGE,"E391"),sQuery(id+"F0.wireOp",EDGE,"E392"),sQuery(id+"F0.wireOp",EDGE,"E393"),sQuery(id+"F0.wireOp",EDGE,"E394"),sQuery(id+"F0.wireOp",EDGE,"E395"),sQuery(id+"F0.wireOp",EDGE,"E396"),sQuery(id+"F0.wireOp",EDGE,"E397"),sQuery(id+"F0.wireOp",EDGE,"E398"),sQuery(id+"F0.wireOp",EDGE,"E399"),sQuery(id+"F0.wireOp",EDGE,"E400"),sQuery(id+"F0.wireOp",EDGE,"E401"),sQuery(id+"F0.wireOp",EDGE,"E402"),sQuery(id+"F0.wireOp",EDGE,"E403"),sQuery(id+"F0.wireOp",EDGE,"E404"),sQuery(id+"F0.wireOp",EDGE,"E405"),sQuery(id+"F0.wireOp",EDGE,"E406"),sQuery(id+"F0.wireOp",EDGE,"E407"),sQuery(id+"F0.wireOp",EDGE,"E408"),sQuery(id+"F0.wireOp",EDGE,"E409"),sQuery(id+"F0.wireOp",EDGE,"E410"),sQuery(id+"F0.wireOp",EDGE,"E411"),sQuery(id+"F0.wireOp",EDGE,"E412"),sQuery(id+"F0.wireOp",EDGE,"E413"),sQuery(id+"F0.wireOp",EDGE,"E414"),sQuery(id+"F0.wireOp",EDGE,"E415"),sQuery(id+"F0.wireOp",EDGE,"E416"),sQuery(id+"F0.wireOp",EDGE,"E417"),sQuery(id+"F0.wireOp",EDGE,"E418"),sQuery(id+"F0.wireOp",EDGE,"E419"),sQuery(id+"F0.wireOp",EDGE,"E420"),sQuery(id+"F0.wireOp",EDGE,"E421"),sQuery(id+"F0.wireOp",EDGE,"E422"),sQuery(id+"F0.wireOp",EDGE,"E423"),sQuery(id+"F0.wireOp",EDGE,"E424"),sQuery(id+"F0.wireOp",EDGE,"E425"),sQuery(id+"F0.wireOp",EDGE,"E426"),sQuery(id+"F0.wireOp",EDGE,"E427"),sQuery(id+"F0.wireOp",EDGE,"E428"),sQuery(id+"F0.wireOp",EDGE,"E429"),sQuery(id+"F0.wireOp",EDGE,"E430"),sQuery(id+"F0.wireOp",EDGE,"E431"),sQuery(id+"F0.wireOp",EDGE,"E432"),sQuery(id+"F0.wireOp",EDGE,"E433"),sQuery(id+"F0.wireOp",EDGE,"E434"),sQuery(id+"F0.wireOp",EDGE,"E435"),sQuery(id+"F0.wireOp",EDGE,"E436"),sQuery(id+"F0.wireOp",EDGE,"E437"),sQuery(id+"F0.wireOp",EDGE,"E438"),sQuery(id+"F0.wireOp",EDGE,"E439"),sQuery(id+"F0.wireOp",EDGE,"E440"),sQuery(id+"F0.wireOp",EDGE,"E441"),sQuery(id+"F0.wireOp",EDGE,"E442")])],"isStart":false});
            var sketch = newSketch(context, id + "F2", { "sketchPlane" : qUnion([Q0])});
            skLineSegment(sketch, "E526", {"start": v(-18.12, 52.26) * mm, "end": v(-2.72, 52.26) * mm});
            skLineSegment(sketch, "E527", {"start": v(-2.72, 52.26) * mm, "end": v(-2.72, 57.25) * mm});
            skLineSegment(sketch, "E528", {"start": v(-2.72, 57.25) * mm, "end": v(9.81, 57.25) * mm});
            skLineSegment(sketch, "E529", {"start": v(9.81, 57.25) * mm, "end": v(9.81, 54.32) * mm});
            skLineSegment(sketch, "E530", {"start": v(9.81, 54.32) * mm, "end": v(15.66, 54.32) * mm});
            skLineSegment(sketch, "E531", {"start": v(15.66, 54.32) * mm, "end": v(15.66, 46.72) * mm});
            skLineSegment(sketch, "E532", {"start": v(15.66, 46.72) * mm, "end": v(7.64, 37.18) * mm});
            skLineSegment(sketch, "E533", {"start": v(7.64, 37.18) * mm, "end": v(-2.52, 37.18) * mm});
            skLineSegment(sketch, "E534", {"start": v(-2.52, 37.18) * mm, "end": v(-2.52, 39.55) * mm});
            skLineSegment(sketch, "E535", {"start": v(-2.52, 39.55) * mm, "end": v(-24.5, 39.55) * mm});
            skLineSegment(sketch, "E536", {"start": v(15.66, 51.29) * mm, "end": v(21.38, 51.29) * mm});
            skLineSegment(sketch, "E537", {"start": v(21.38, 51.29) * mm, "end": v(21.38, 60.62) * mm});
            skSolve(sketch);
        }
        {
            var Q0;
            Q0=makeQuery(id+"F2.imprint","IMPRINT",FACE,{"disambiguationData":[TD([[makeQuery(id+"F2.imprint","IMPRINT",EDGE,{"derivedFrom":sQuery(id+"F2.wireOp",EDGE,"E526")}),1.0]])]});
            var Q1;
            {var subQ3=sQuery(id+"F2.wireOp",EDGE,"E532");Q1=makeQuery(id+"F2.imprint","IMPRINT",FACE,{"disambiguationData":[TD([[makeQuery(id+"F2.imprint","IMPRINT",EDGE,{"derivedFrom":subQ3}),1.0]])]});}
            extrude(context, id + "F3", {"entities" : qUnion([Q0, Q1]), "operationType" : NewBodyOperationType.REMOVE, "oppositeDirection" : true, "depth" : 25 * mm, "offsetDistance" : 25 * mm});
        }
    });
